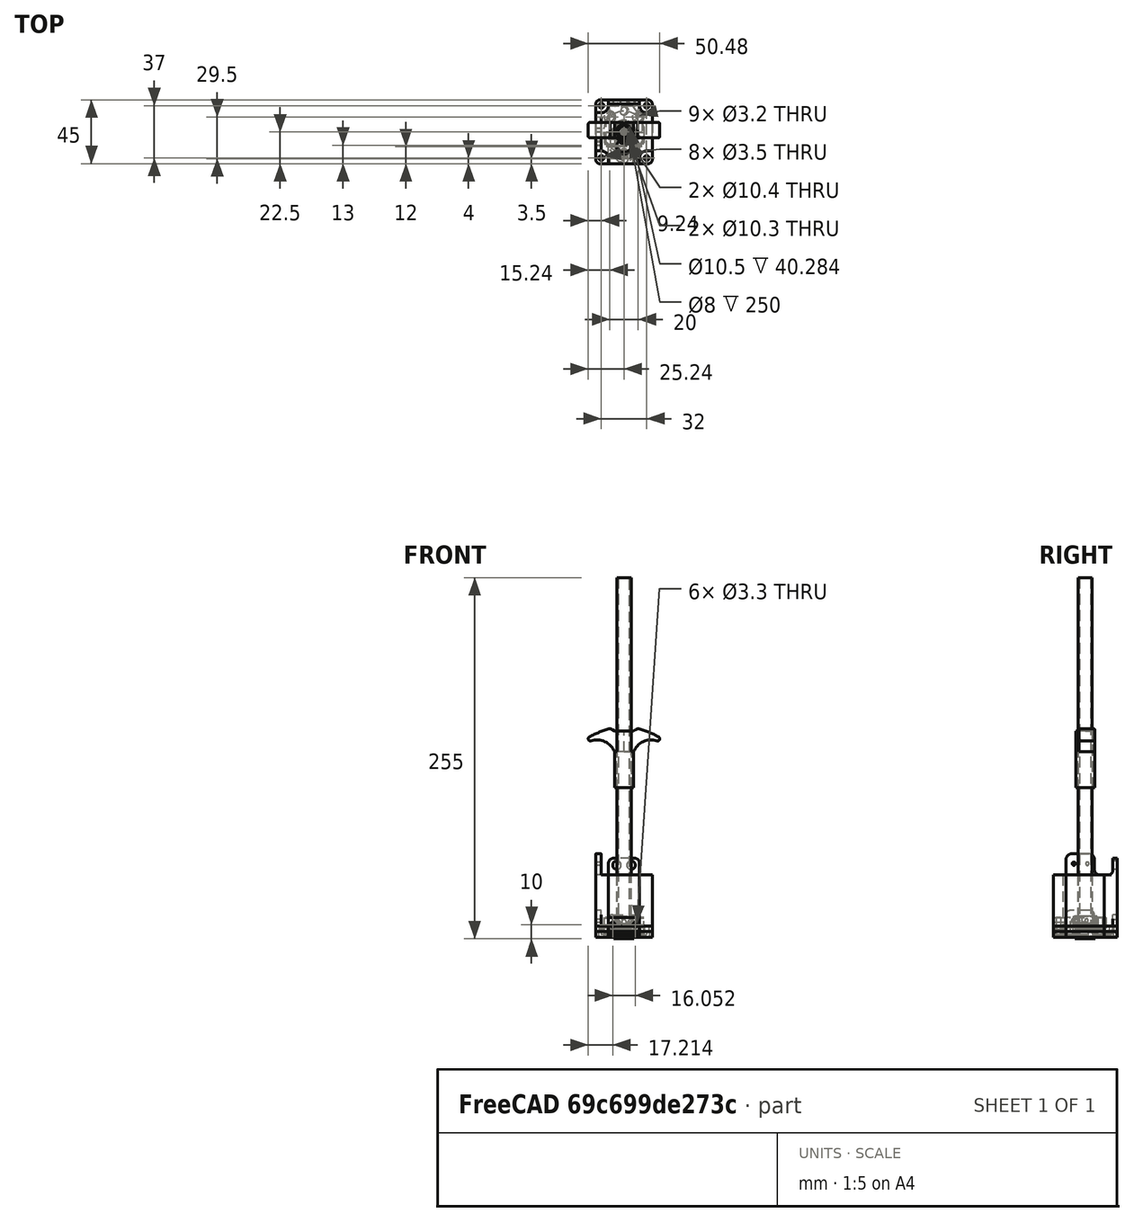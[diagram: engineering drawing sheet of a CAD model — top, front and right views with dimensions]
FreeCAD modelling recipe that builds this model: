
FCSTD DOCUMENT  (FreeCAD 1.0R39109 (Git))
Label: AltGearHandle
License: All rights reserved
LicenseURL: http://en.wikipedia.org/wiki/All_rights_reserved
objects: Sketcher::SketchObject×36, PartDesign::Pad×15, PartDesign::Body×14, PartDesign::Pocket×12, App::Link×9, App::FeaturePython×9, PartDesign::Fillet×8, PartDesign::Revolution×6, PartDesign::Chamfer×3, PartDesign::Hole×2, PartDesign::Mirrored×2, PartDesign::Plane×2, Part::Part2DObjectPython×2, Assembly::JointGroup×1, Assembly::AssemblyObject×1
note: 232 computed .brp shape members not serialized (recipe doc carries the construction recipe); baked Part::Feature solids carry a one-line shape summary decoded from their .brp

FEATURE [Sketcher::SketchObject] Sketch
  ArcFitTolerance = 0
  AttachmentSupport = -> [XY_Plane]
  FullyConstrained = true
  MakeInternals = false
  MapMode = 5
  sketch-geometry (11):
    g0: LineSegment StartX=-12.7 StartY=8.1026 StartZ=0 EndX=-5.7589 EndY=18.8369 EndZ=0
    g1: ArcOfCircle CenterX=0 CenterY=15.113 CenterZ=0 NormalX=0 NormalY=0 NormalZ=1 AngleXU=0 Radius=6.858 StartAngle=0.574002 EndAngle=2.56759
    g2: LineSegment StartX=5.7589 StartY=18.8369 StartZ=0 EndX=12.7 EndY=8.1026 EndZ=0
    g3: LineSegment StartX=12.7 StartY=8.1026 StartZ=0 EndX=12.7 EndY=-8.1026 EndZ=0
    g4: LineSegment StartX=12.7 StartY=-8.1026 StartZ=0 EndX=5.7589 EndY=-18.8369 EndZ=0
    g5: ArcOfCircle CenterX=0 CenterY=-15.113 CenterZ=0 NormalX=0 NormalY=0 NormalZ=1 AngleXU=0 Radius=6.858 StartAngle=3.71559 EndAngle=5.70918
    g6: LineSegment StartX=-5.7589 StartY=-18.8369 StartZ=0 EndX=-12.7 EndY=-8.1026 EndZ=0
    g7: LineSegment StartX=-12.7 StartY=-8.1026 StartZ=0 EndX=-12.7 EndY=8.1026 EndZ=0
    g8: LineSegment [constr] StartX=0 StartY=21.971 StartZ=0 EndX=12.7 EndY=21.971 EndZ=0
    g9: Circle CenterX=2.5146 CenterY=-3.2766 CenterZ=0 NormalX=0 NormalY=0 NormalZ=1 AngleXU=0 Radius=5.5
    g10: LineSegment [constr] StartX=0 StartY=-21.971 StartZ=0 EndX=12.7 EndY=-21.971 EndZ=0
  constraints (30):
    c: Tangent(g0,g1) = 1.5708
    c: Tangent(g1,g2) = 1.5708
    c: Coincident(g2,g3)
    c: Coincident(g3,g4)
    c: Tangent(g4,g5) = 1.5708
    c: Tangent(g5,g6) = 1.5708
    c: Coincident(g6,g7)
    c: Coincident(g7,g0)
    c: Vertical(g7)
    c: PointOnObject(g1,g-2)
    c: Equal(g5,g1)
    c: PointOnObject(g8,g-2)
    c: Horizontal(g8)
    c: Vertical(g8,g2)
    c: Tangent(g8,g1)
    c: DistanceY(g8) = 21.971
    c: Symmetric(g1,g5,g-1)
    c: Symmetric(g0,g2,g-2)
    c: Equal(g7,g3)
    c: Symmetric(g3,g2,g-1)
    c: Radius(g5) = 6.858
    c: DistanceY(g2,g8) = 13.8684
    c: DistanceX(g6,g3) = 25.4
    c: DistanceX(g9,g3) = 10.1854
    c: Diameter(g9) = 11
    c: PointOnObject(g10,g-2)
    c: Horizontal(g10)
    c: Equal(g10,g8)
    c: Tangent(g10,g5)
    c: DistanceY(g10,g9) = 18.6944
FEATURE [PartDesign::Pad] Pad  label="BasePad"
  Direction = (0,0,1)
  Length = 3.17
  Length2 = 10
  Profile = -> Sketch
  ReferenceAxis = -> Sketch [N_Axis]
  Reversed = true
  Suppressed = false
  Type = 0
FEATURE [Sketcher::SketchObject] Sketch001
  ArcFitTolerance = 0
  AttachmentSupport = -> [XY_Plane]
  ExternalGeometry = -> [Pad]
  FullyConstrained = true
  MakeInternals = false
  MapMode = 5
  sketch-geometry (3):
    g0: Circle CenterX=0 CenterY=15.113 CenterZ=0 NormalX=0 NormalY=0 NormalZ=1 AngleXU=0 Radius=2.3114
    g1: Circle CenterX=0 CenterY=-15.113 CenterZ=0 NormalX=0 NormalY=0 NormalZ=1 AngleXU=0 Radius=2.3114
    g2: LineSegment [constr] StartX=0 StartY=21.971 StartZ=0 EndX=5.7589 EndY=21.971 EndZ=0
  constraints (9):
    c: PointOnObject(g0,g-2)
    c: Horizontal(g2)
    c: PointOnObject(g2,g-2)
    c: Vertical(g2,g-3)
    c: Tangent(g2,g-3)
    c: Equal(g0,g1)
    c: Diameter(g0) = 4.6228
    c: Symmetric(g0,g1,g-1)
    c: DistanceY(g0,g2) = 6.858
FEATURE [PartDesign::Hole] Hole
  BaseFeature = -> Pad
  CustomThreadClearance = 0
  Depth = 25
  DepthType = 0
  Diameter = 4.5
  DrillForDepth = false
  DrillPoint = 1
  DrillPointAngle = 118
  HoleCutCountersinkAngle = 90
  HoleCutCustomValues = false
  HoleCutDepth = 0
  HoleCutDiameter = 6.3
  HoleCutType = 2
  ModelThread = false
  Profile = -> Sketch001
  Suppressed = false
  Tapered = false
  TaperedAngle = 90
  ThreadClass = 0
  ThreadDepth = 25
  ThreadDepthType = 0
  ThreadDirection = 0
  ThreadFit = 0
  ThreadSize = 11
  ThreadType = 1
  Threaded = false
  UseCustomThreadClearance = false
FEATURE [PartDesign::Fillet] Fillet
  Base = -> Hole [Edge13,Edge14,Edge6,Edge3]
  BaseFeature = -> Hole
  Radius = 1
  SupportTransform = false
  Suppressed = false
  UseAllEdges = false
FEATURE [PartDesign::Body] Body  label="mountingPlate"
  AllowCompound = false
  Group = -> [Sketch,Pad,Sketch001,Hole,Fillet]
  Origin = -> Origin
  Tip = -> Fillet
FEATURE [Sketcher::SketchObject] Sketch002  label="mastersketch"
  ArcFitTolerance = 0
  AttachmentSupport = -> [XZ_Plane001]
  FullyConstrained = false
  MakeInternals = false
  MapMode = 5
  Placement = pos=(0,0,0) rot=(1,0,0;1.5708rad)
  sketch-geometry (21):
    g0: LineSegment StartX=-5 StartY=101.6 StartZ=0 EndX=5 EndY=101.6 EndZ=0
    g1: LineSegment StartX=5 StartY=101.6 StartZ=0 EndX=5 EndY=-60 EndZ=0
    g2: LineSegment StartX=5 StartY=-60 StartZ=0 EndX=-5 EndY=-60 EndZ=0
    g3: LineSegment StartX=-5 StartY=-60 StartZ=0 EndX=-5 EndY=101.6 EndZ=0
    g4: LineSegment [constr] StartX=-25.4 StartY=0 StartZ=0 EndX=-25.4 EndY=147.32 EndZ=0
    g5: LineSegment [constr] StartX=25.4 StartY=0 StartZ=0 EndX=25.4 EndY=147.32 EndZ=0
    g6: LineSegment StartX=-6.70052 StartY=141.884 StartZ=0 EndX=6.70052 EndY=141.884 EndZ=0
    g7: LineSegment StartX=6.70052 StartY=141.884 StartZ=0 EndX=6.70052 EndY=101.6 EndZ=0
    g8: LineSegment StartX=6.70052 StartY=101.6 StartZ=0 EndX=-6.70052 EndY=101.6 EndZ=0
    g9: LineSegment StartX=-6.70052 StartY=101.6 StartZ=0 EndX=-6.70052 EndY=141.884 EndZ=0
    g10: ArcOfCircle CenterX=-19.1442 CenterY=122.136 CenterZ=0 NormalX=0 NormalY=0 NormalZ=1 AngleXU=0 Radius=13.3604 StartAngle=0.3726 EndAngle=1.90028
    g11: ArcOfCircle CenterX=-23.9395 CenterY=136.16 CenterZ=0 NormalX=0 NormalY=0 NormalZ=1 AngleXU=0 Radius=1.4605 StartAngle=1.94929 EndAngle=5.04187
    g12: LineSegment StartX=-24.4792 StartY=137.517 StartZ=0 EndX=-9.6647 EndY=143.408 EndZ=0
    g13: LineSegment StartX=-9.6647 StartY=143.408 StartZ=0 EndX=-6.70052 EndY=141.884 EndZ=0
    g14: LineSegment StartX=-6.70052 StartY=141.884 StartZ=0 EndX=-6.70052 EndY=127 EndZ=0
    g15: LineSegment StartX=6.70052 StartY=128.917 StartZ=0 EndX=6.70052 EndY=141.884 EndZ=0
    g16: LineSegment StartX=6.70052 StartY=141.884 StartZ=0 EndX=9.6647 EndY=143.408 EndZ=0
    g17: LineSegment StartX=9.6647 StartY=143.408 StartZ=0 EndX=24.4792 EndY=137.517 EndZ=0
    g18: ArcOfCircle CenterX=23.9395 CenterY=136.16 CenterZ=0 NormalX=0 NormalY=0 NormalZ=1 AngleXU=0 Radius=1.4605 StartAngle=4.38291 EndAngle=7.47549
    g19: ArcOfCircle CenterX=19.1442 CenterY=122.136 CenterZ=0 NormalX=0 NormalY=0 NormalZ=1 AngleXU=0 Radius=13.3604 StartAngle=1.24132 EndAngle=2.76899
    g20: LineSegment StartX=6.70052 StartY=127 StartZ=0 EndX=6.70052 EndY=141.884 EndZ=0
  constraints (58):
    c: Coincident(g0,g1)
    c: Coincident(g1,g2)
    c: Coincident(g2,g3)
    c: Coincident(g3,g0)
    c: Horizontal(g0)
    c: Vertical(g1)
    c: Vertical(g3)
    c: Symmetric(g2,g1,g-2)
    c: DistanceX(g2,g2) = 10
    c: DistanceY(g0) = 101.6
    c: DistanceY(g1) = -60
    c: PointOnObject(g4,g-1)
    c: Vertical(g4)
    c: PointOnObject(g5,g-1)
    c: Vertical(g5)
    c: Symmetric(g5,g4,g-2)
    c: DistanceX(g4,g5) = 50.8
    c: DistanceY(g0,g5) = 45.72
    c: Coincident(g6,g7)
    c: Coincident(g7,g8)
    c: Coincident(g8,g9)
    c: Coincident(g9,g6)
    c: Horizontal(g6)
    c: Vertical(g7)
    c: Vertical(g9)
    c: Horizontal(g0,g7)
    c: Symmetric(g8,g7,g-2)
    c: DistanceX(g8,g8) = 13.401
    c: DistanceY(g6,g5) = 5.4356
    c: PointOnObject(g10,g9)
    c: Tangent(g10,g11) = 1.5708
    c: Tangent(g11,g12) = 1.5708
    c: Coincident(g12,g13)
    c: Coincident(g13,g14)
    c: Coincident(g14,g10)
    c: PointOnObject(g15,g7)
    c: PointOnObject(g15,g7)
    c: Coincident(g15,g16)
    c: Coincident(g16,g17)
    c: Tangent(g17,g18) = 1.5708
    c: Tangent(g18,g19) = 1.5708
    c: PointOnObject(g19,g7)
    c: Coincident(g20,g19)
    c: Coincident(g20,g15)
    c: Horizontal(g19,g10)
    c: Equal(g10,g19)
    c: Equal(g18,g11)
    c: Tangent(g18,g5)
    c: Symmetric(g18,g11,g-2)
    c: Horizontal(g13,g15)
    c: Symmetric(g16,g12,g-2)
    c: Radius(g19) = 13.3604
    c: Radius(g18) = 1.4605
    c: DistanceY(g8,g10) = 25.4
    c: DistanceY(g6,g16) = 1.524
    c: Coincident(g13,g6)
    c: DistanceX(g12,g16) = 19.3294
    c: DistanceY(g10,g11) = 9.16
FEATURE [Sketcher::SketchObject] Sketch004
  ArcFitTolerance = 0
  AttachmentOffset = pos=(0,0,-6.7) rot=(0,0,1;0rad)
  AttachmentSupport = -> [XZ_Plane001]
  ExternalGeometry = -> [Sketch002]
  FullyConstrained = true
  MakeInternals = false
  MapMode = 5
  Placement = pos=(0,6.7,-1.5e-15) rot=(1,0,0;1.5708rad)
  sketch-geometry (7):
    g0: LineSegment StartX=-6.70052 StartY=141.884 StartZ=0 EndX=-9.6647 EndY=143.408 EndZ=0
    g1: ArcOfCircle CenterX=-19.1442 CenterY=122.136 CenterZ=0 NormalX=0 NormalY=0 NormalZ=1 AngleXU=0 Radius=13.3604 StartAngle=0.3726 EndAngle=1.8879
    g2: LineSegment StartX=-6.70052 StartY=141.884 StartZ=0 EndX=0 EndY=141.884 EndZ=0
    g3: LineSegment StartX=0 StartY=141.884 StartZ=0 EndX=0 EndY=127 EndZ=0
    g4: LineSegment StartX=0 StartY=127 StartZ=0 EndX=-6.70052 EndY=127 EndZ=0
    g5: ArcOfCircle CenterX=6.31595 CenterY=81.6504 CenterZ=0 NormalX=0 NormalY=0 NormalZ=1 AngleXU=0 Radius=63.7921 StartAngle=1.824 EndAngle=2.07458
    g6: ArcOfCircle CenterX=-23.7689 CenterY=136.229 CenterZ=0 NormalX=0 NormalY=0 NormalZ=1 AngleXU=0 Radius=1.47134 StartAngle=2.07458 EndAngle=5.02949
  constraints (18):
    c: Coincident(g1,g-4)
    c: Coincident(g0,g-6)
    c: Parallel(g-6,g0)
    c: Coincident(g1,g-4)
    c: Coincident(g0,g2)
    c: Horizontal(g2)
    c: Coincident(g2,g3)
    c: Vertical(g3)
    c: Coincident(g3,g4)
    c: Coincident(g4,g1)
    c: Horizontal(g4)
    c: Horizontal(g0,g-6)
    c: PointOnObject(g2,g-2)
    c: Coincident(g5,g0)
    c: Radius(g5) = 63.7921
    c: Tangent(g6,g5) = -1.5708
    c: Tangent(g6,g1) = 1.5708
    c: Coincident(g-5,g5)
FEATURE [PartDesign::Pad] Pad001  label="gripBase1"
  Direction = (0,-1,2e-16)
  Length = 11
  Length2 = 10
  Placement = pos=(0,0,0) rot=(1,0,0;1.5708rad)
  Profile = -> Sketch004
  ReferenceAxis = -> Sketch004 [N_Axis]
  Suppressed = false
  Type = 0
FEATURE [PartDesign::Mirrored] Mirrored
  BaseFeature = -> Pad001
  MirrorPlane = -> Sketch004 [V_Axis]
  Originals = -> [Pad001]
  Placement = pos=(0,0,0) rot=(1,0,0;1.5708rad)
  Suppressed = false
  TransformMode = 0
FEATURE [PartDesign::Fillet] Fillet001  label="Grip"
  Base = -> Mirrored [Edge25,Edge29,Edge16,Edge11]
  BaseFeature = -> Mirrored
  Placement = pos=(0,0,0) rot=(1,0,0;1.5708rad)
  Radius = 1.2
  SupportTransform = false
  Suppressed = false
  UseAllEdges = false
FEATURE [Sketcher::SketchObject] Sketch005
  ArcFitTolerance = 0
  AttachmentSupport = -> [XZ_Plane001]
  ExternalGeometry = -> [Sketch002]
  FullyConstrained = true
  MakeInternals = false
  MapMode = 5
  Placement = pos=(0,0,0) rot=(1,0,0;1.5708rad)
  sketch-geometry (4):
    g0: LineSegment StartX=-6.70052 StartY=141.884 StartZ=0 EndX=0 EndY=141.884 EndZ=0
    g1: LineSegment StartX=0 StartY=141.884 StartZ=0 EndX=0 EndY=101.6 EndZ=0
    g2: LineSegment StartX=0 StartY=101.6 StartZ=0 EndX=-6.70052 EndY=101.6 EndZ=0
    g3: LineSegment StartX=-6.70052 StartY=101.6 StartZ=0 EndX=-6.70052 EndY=141.884 EndZ=0
  constraints (11):
    c: Coincident(g0,g1)
    c: Coincident(g1,g2)
    c: Coincident(g2,g3)
    c: Coincident(g3,g0)
    c: Horizontal(g0)
    c: Horizontal(g2)
    c: Vertical(g1)
    c: Vertical(g3)
    c: Coincident(g0,g-3)
    c: PointOnObject(g1,g-2)
    c: Horizontal(g-3,g1)
FEATURE [PartDesign::Revolution] Revolution
  Angle = 360
  Angle2 = 60
  Axis = (0,2e-16,1)
  Base = (0,0,0)
  BaseFeature = -> Fillet001
  Placement = pos=(0,0,0) rot=(1,0,0;1.5708rad)
  Profile = -> Sketch005
  ReferenceAxis = -> Sketch005 [V_Axis]
  Suppressed = false
  Type = 0
FEATURE [Sketcher::SketchObject] Sketch006
  ArcFitTolerance = 0
  AttachmentSupport = -> [XY_Plane001]
  ExternalGeometry = -> [Sketch002]
  FullyConstrained = true
  MakeInternals = false
  MapMode = 5
  sketch-geometry (1):
    g0: Circle CenterX=0 CenterY=0 CenterZ=0 NormalX=0 NormalY=0 NormalZ=1 AngleXU=0 Radius=5.25
  constraints (2):
    c: Coincident(g0,g-1)
    c: Diameter(g0) = 10.5
FEATURE [PartDesign::Pocket] Pocket
  BaseFeature = -> Revolution
  Direction = (0,0,-1)
  Length = 5
  Length2 = 5
  Midplane = true
  Placement = pos=(0,0,0) rot=(1,0,0;1.5708rad)
  Profile = -> Sketch006
  ReferenceAxis = -> Sketch006 [N_Axis]
  Suppressed = false
  Type = 1
FEATURE [PartDesign::Plane] DatumPlane
  AttachmentSupport = -> [Pocket]
  Length = 60.0479
  MapMode = 45
  Placement = pos=(0,6.70021,141.884) rot=(0,0,1;1.5708rad)
  ResizeMode = 0
  Width = 60.5283
FEATURE [PartDesign::Plane] DatumPlane001
  AttachmentSupport = -> [Pocket]
  Length = 193.249
  MapMode = 45
  Placement = pos=(-24.6781,1.2,135.833) rot=(0.548172,0,0.836366;3.14159rad)
  ResizeMode = 0
  Width = 68.6849
FEATURE [PartDesign::Body] Body001  label="Handle"
  AllowCompound = false
  Group = -> [Sketch002,Sketch004,Pad001,Mirrored,Fillet001,Sketch005,Revolution,Sketch006,Pocket,DatumPlane,DatumPlane001]
  Origin = -> Origin001
  Tip = -> Pocket
FEATURE [Sketcher::SketchObject] Sketch008
  ArcFitTolerance = 1e-06
  AttachmentSupport = -> [XZ_Plane003]
  FullyConstrained = true
  MakeInternals = false
  MapMode = 5
  Placement = pos=(0,0,0) rot=(1,0,0;1.5708rad)
  sketch-geometry (12):
    g0: LineSegment StartX=-3.6 StartY=0 StartZ=0 EndX=-3.6 EndY=2.452 EndZ=0
    g1: LineSegment StartX=-3.6 StartY=2.452 StartZ=0 EndX=-4.699 EndY=2.452 EndZ=0
    g2: LineSegment StartX=-4.699 StartY=2.452 StartZ=0 EndX=-4.699 EndY=5.5 EndZ=0
    g3: LineSegment StartX=-4.699 StartY=5.5 StartZ=0 EndX=0 EndY=5.5 EndZ=0
    g4: LineSegment StartX=0 StartY=5.5 StartZ=0 EndX=0 EndY=4 EndZ=0
    g5: LineSegment StartX=0 StartY=4 StartZ=0 EndX=-1.3 EndY=4 EndZ=0
    g6: LineSegment StartX=-1.3 StartY=4 StartZ=0 EndX=-1.3 EndY=1 EndZ=0
    g7: LineSegment StartX=-1.3 StartY=1 StartZ=0 EndX=-2.3 EndY=1 EndZ=0
    g8: LineSegment StartX=-2.3 StartY=1 StartZ=0 EndX=-2.3 EndY=4 EndZ=0
    g9: LineSegment StartX=-2.3 StartY=4 StartZ=0 EndX=-3.1 EndY=4 EndZ=0
    g10: LineSegment StartX=-3.1 StartY=4 StartZ=0 EndX=-3.1 EndY=0 EndZ=0
    g11: LineSegment StartX=-3.1 StartY=0 StartZ=0 EndX=-3.6 EndY=0 EndZ=0
  constraints (36):
    c: PointOnObject(g0,g-1)
    c: Vertical(g0)
    c: Coincident(g0,g1)
    c: Horizontal(g1)
    c: Coincident(g1,g2)
    c: Vertical(g2)
    c: Coincident(g2,g3)
    c: PointOnObject(g3,g-2)
    c: Horizontal(g3)
    c: Coincident(g3,g4)
    c: Vertical(g4)
    c: Coincident(g4,g5)
    c: Coincident(g5,g6)
    c: Coincident(g6,g7)
    c: Coincident(g7,g8)
    c: Vertical(g8)
    c: Coincident(g8,g9)
    c: Coincident(g9,g10)
    c: Vertical(g10)
    c: Coincident(g10,g11)
    c: Coincident(g11,g0)
    c: Horizontal(g11)
    c: Horizontal(g7)
    c: Vertical(g6)
    c: Horizontal(g5)
    c: DistanceY(g2,g2) = 3.048
    c: Horizontal(g5,g8)
    c: Horizontal(g9)
    c: DistanceY(g6,g6) = 3
    c: DistanceX(g5,g5) = 1.3
    c: DistanceX(g3,g3) = 4.699
    c: DistanceX(g7,g7) = 1
    c: DistanceY(g4,g4) = 1.5
    c: DistanceY(g10,g7) = 1
    c: DistanceX(g9,g9) = 0.8
    c: DistanceX(g11,g11) = 0.5
FEATURE [Sketcher::SketchObject] Sketch009
  ArcFitTolerance = 1e-06
  AttachmentSupport = -> [XZ_Plane002]
  FullyConstrained = true
  MakeInternals = false
  MapMode = 5
  Placement = pos=(0,0,0) rot=(1,0,0;1.5708rad)
  sketch-geometry (6):
    g0: LineSegment StartX=-3.25 StartY=0 StartZ=0 EndX=-3.25 EndY=6 EndZ=0
    g1: LineSegment StartX=-5.1 StartY=4.476 StartZ=0 EndX=-4.9 EndY=0 EndZ=0
    g2: LineSegment StartX=-4.9 StartY=0 StartZ=0 EndX=-3.25 EndY=0 EndZ=0
    g3: LineSegment StartX=-5.1 StartY=4.476 StartZ=0 EndX=-6 EndY=4.476 EndZ=0
    g4: LineSegment StartX=-6 StartY=4.476 StartZ=0 EndX=-6 EndY=6 EndZ=0
    g5: LineSegment StartX=-6 StartY=6 StartZ=0 EndX=-3.25 EndY=6 EndZ=0
  constraints (18):
    c: PointOnObject(g2,g-1)
    c: PointOnObject(g1,g-1)
    c: Coincident(g1,g2)
    c: Coincident(g1,g3)
    c: Coincident(g3,g4)
    c: Vertical(g4)
    c: Horizontal(g3)
    c: DistanceY(g4,g4) = 1.524
    c: DistanceX(g1) = -4.9
    c: DistanceX(g1) = -5.1
    c: DistanceX(g4) = -6
    c: Coincident(g0,g2)
    c: Vertical(g0)
    c: Coincident(g5,g4)
    c: Coincident(g5,g0)
    c: Horizontal(g5)
    c: DistanceX(g0) = -3.25
    c: DistanceY(g0,g0) = 6
FEATURE [PartDesign::Revolution] Revolution001
  Angle = 360
  Angle2 = 60
  Axis = (0,2e-16,1)
  Base = (0,0,0)
  Placement = pos=(0,0,0) rot=(1,0,0;1.5708rad)
  Profile = -> Sketch009
  ReferenceAxis = -> Sketch009 [V_Axis]
  Suppressed = false
  Type = 0
FEATURE [PartDesign::Body] Body002  label="TopNut"
  AllowCompound = false
  Group = -> [Sketch009,Revolution001]
  Origin = -> Origin002
  Tip = -> Revolution001
FEATURE [PartDesign::Revolution] Revolution002
  Angle = 360
  Angle2 = 60
  Axis = (0,2e-16,1)
  Base = (0,0,0)
  Placement = pos=(0,0,0) rot=(1,0,0;1.5708rad)
  Profile = -> Sketch008
  ReferenceAxis = -> Sketch008 [V_Axis]
  Suppressed = false
  Type = 0
FEATURE [Sketcher::SketchObject] Sketch010
  ArcFitTolerance = 1e-06
  AttachmentSupport = -> [XY_Plane003]
  FullyConstrained = true
  MakeInternals = false
  MapMode = 5
  sketch-geometry (4):
    g0: LineSegment StartX=-0.25 StartY=2.5 StartZ=0 EndX=-0.25 EndY=-2.5 EndZ=0
    g1: LineSegment StartX=-0.25 StartY=-2.5 StartZ=0 EndX=0.25 EndY=-2.5 EndZ=0
    g2: LineSegment StartX=0.25 StartY=-2.5 StartZ=0 EndX=0.25 EndY=2.5 EndZ=0
    g3: LineSegment StartX=0.25 StartY=2.5 StartZ=0 EndX=-0.25 EndY=2.5 EndZ=0
  constraints (11):
    c: Coincident(g0,g1)
    c: Coincident(g1,g2)
    c: Coincident(g2,g3)
    c: Coincident(g3,g0)
    c: Vertical(g0)
    c: Vertical(g2)
    c: Horizontal(g1)
    c: Horizontal(g3)
    c: Symmetric(g0,g2,g-1)
    c: DistanceY(g2,g2) = 5
    c: DistanceX(g1,g1) = 0.5
FEATURE [PartDesign::Pocket] Pocket001
  BaseFeature = -> Revolution002
  Direction = (0,0,-1)
  Length = 0
  Length2 = 5
  Placement = pos=(0,0,0) rot=(1,0,0;1.5708rad)
  Profile = -> Sketch010
  ReferenceAxis = -> Sketch010 [N_Axis]
  Reversed = true
  Suppressed = false
  Type = 3
  UpToFace = -> Revolution002 [Face5]
FEATURE [PartDesign::Chamfer] Chamfer
  Angle = 45
  Base = -> Pocket001 [Edge8,Edge5,Edge42,Edge29]
  BaseFeature = -> Pocket001
  ChamferType = 0
  FlipDirection = false
  Placement = pos=(0,0,0) rot=(1,0,0;1.5708rad)
  Size = 0.3
  Size2 = 1
  SupportTransform = false
  Suppressed = false
  UseAllEdges = false
FEATURE [PartDesign::Body] Body003  label="Button"
  AllowCompound = false
  Group = -> [Sketch008,Revolution002,Sketch010,Pocket001,Chamfer]
  Origin = -> Origin003
  Tip = -> Chamfer
FEATURE [Sketcher::SketchObject] Sketch011
  ArcFitTolerance = 1e-06
  AttachmentSupport = -> [XZ_Plane004]
  FullyConstrained = true
  MakeInternals = false
  MapMode = 5
  Placement = pos=(0,0,0) rot=(1,0,0;1.5708rad)
  sketch-geometry (12):
    g0: LineSegment StartX=-3.45 StartY=0 StartZ=0 EndX=-3.45 EndY=1.452 EndZ=0
    g1: LineSegment StartX=-3.45 StartY=1.452 StartZ=0 EndX=-4.699 EndY=1.452 EndZ=0
    g2: LineSegment StartX=-4.699 StartY=1.452 StartZ=0 EndX=-4.699 EndY=4.5 EndZ=0
    g3: LineSegment StartX=-4.699 StartY=4.5 StartZ=0 EndX=0 EndY=4.5 EndZ=0
    g4: LineSegment StartX=0 StartY=4.5 StartZ=0 EndX=0 EndY=3 EndZ=0
    g5: LineSegment StartX=0 StartY=3 StartZ=0 EndX=-1.15 EndY=3 EndZ=0
    g6: LineSegment StartX=-1.15 StartY=3 StartZ=0 EndX=-1.15 EndY=0 EndZ=0
    g7: LineSegment StartX=-1.15 StartY=0 StartZ=0 EndX=-2.15 EndY=0 EndZ=0
    g8: LineSegment StartX=-2.15 StartY=0 StartZ=0 EndX=-2.15 EndY=3 EndZ=0
    g9: LineSegment StartX=-2.15 StartY=3 StartZ=0 EndX=-2.95 EndY=3 EndZ=0
    g10: LineSegment StartX=-2.95 StartY=3 StartZ=0 EndX=-2.95 EndY=0 EndZ=0
    g11: LineSegment StartX=-2.95 StartY=0 StartZ=0 EndX=-3.45 EndY=0 EndZ=0
  constraints (36):
    c: Vertical(g0)
    c: Coincident(g0,g1)
    c: Horizontal(g1)
    c: Coincident(g1,g2)
    c: Vertical(g2)
    c: Coincident(g2,g3)
    c: PointOnObject(g3,g-2)
    c: Horizontal(g3)
    c: Coincident(g3,g4)
    c: Vertical(g4)
    c: Coincident(g4,g5)
    c: Coincident(g5,g6)
    c: Coincident(g6,g7)
    c: Coincident(g7,g8)
    c: Vertical(g8)
    c: Coincident(g8,g9)
    c: Coincident(g9,g10)
    c: Vertical(g10)
    c: Coincident(g10,g11)
    c: Coincident(g11,g0)
    c: Horizontal(g11)
    c: Horizontal(g7)
    c: Vertical(g6)
    c: Horizontal(g5)
    c: DistanceY(g2,g2) = 3.048
    c: Horizontal(g5,g8)
    c: Horizontal(g9)
    c: DistanceY(g6,g6) = 3
    c: DistanceX(g5,g5) = 1.15
    c: DistanceX(g3,g3) = 4.699
    c: DistanceX(g7,g7) = 1
    c: DistanceY(g4,g4) = 1.5
    c: DistanceX(g9,g9) = 0.8
    c: DistanceX(g11,g11) = 0.5
    c: Horizontal(g10,g7)
    c: PointOnObject(g10,g-1)
FEATURE [PartDesign::Revolution] Revolution003
  Angle = 360
  Angle2 = 60
  Axis = (0,2e-16,1)
  Base = (0,0,0)
  Placement = pos=(0,0,0) rot=(1,0,0;1.5708rad)
  Profile = -> Sketch011
  ReferenceAxis = -> Sketch011 [V_Axis]
  Suppressed = false
  Type = 0
FEATURE [Sketcher::SketchObject] Sketch012
  ArcFitTolerance = 1e-06
  AttachmentSupport = -> [XY_Plane004]
  FullyConstrained = true
  MakeInternals = false
  MapMode = 5
  sketch-geometry (4):
    g0: LineSegment StartX=-0.25 StartY=2.5 StartZ=0 EndX=-0.25 EndY=-2.5 EndZ=0
    g1: LineSegment StartX=-0.25 StartY=-2.5 StartZ=0 EndX=0.25 EndY=-2.5 EndZ=0
    g2: LineSegment StartX=0.25 StartY=-2.5 StartZ=0 EndX=0.25 EndY=2.5 EndZ=0
    g3: LineSegment StartX=0.25 StartY=2.5 StartZ=0 EndX=-0.25 EndY=2.5 EndZ=0
  constraints (11):
    c: Coincident(g0,g1)
    c: Coincident(g1,g2)
    c: Coincident(g2,g3)
    c: Coincident(g3,g0)
    c: Vertical(g0)
    c: Vertical(g2)
    c: Horizontal(g1)
    c: Horizontal(g3)
    c: Symmetric(g0,g2,g-1)
    c: DistanceY(g2,g2) = 5
    c: DistanceX(g1,g1) = 0.5
FEATURE [PartDesign::Pocket] Pocket002
  BaseFeature = -> Revolution003
  Direction = (0,0,-1)
  Length = 0
  Length2 = 5
  Placement = pos=(0,0,0) rot=(1,0,0;1.5708rad)
  Profile = -> Sketch012
  ReferenceAxis = -> Sketch012 [N_Axis]
  Reversed = true
  Suppressed = false
  Type = 3
  UpToFace = -> Revolution003 [Face5]
FEATURE [PartDesign::Chamfer] Chamfer001
  Angle = 45
  Base = -> Pocket002 [Edge8,Edge5,Edge42,Edge29]
  BaseFeature = -> Pocket002
  ChamferType = 0
  FlipDirection = false
  Placement = pos=(0,0,0) rot=(1,0,0;1.5708rad)
  Size = 0.3
  Size2 = 1
  SupportTransform = false
  Suppressed = false
  UseAllEdges = false
FEATURE [PartDesign::Body] Body004  label="Button2"
  AllowCompound = false
  Group = -> [Sketch011,Revolution003,Sketch012,Pocket002,Chamfer001]
  Origin = -> Origin004
  Tip = -> Chamfer001
FEATURE [Sketcher::SketchObject] Sketch013
  ArcFitTolerance = 1e-06
  AttachmentSupport = -> [XY_Plane005]
  FullyConstrained = true
  MakeInternals = false
  MapMode = 5
  sketch-geometry (13):
    g0: LineSegment StartX=-20 StartY=22.5 StartZ=0 EndX=-20 EndY=-22.5 EndZ=0
    g1: LineSegment StartX=-20 StartY=-22.5 StartZ=0 EndX=20 EndY=-22.5 EndZ=0
    g2: LineSegment StartX=20 StartY=-22.5 StartZ=0 EndX=20 EndY=22.5 EndZ=0
    g3: LineSegment StartX=20 StartY=22.5 StartZ=0 EndX=-20 EndY=22.5 EndZ=0
    g4: LineSegment [constr] StartX=-16 StartY=18.5 StartZ=0 EndX=-16 EndY=-18.5 EndZ=0
    g5: LineSegment [constr] StartX=-16 StartY=-18.5 StartZ=0 EndX=16 EndY=-18.5 EndZ=0
    g6: LineSegment [constr] StartX=16 StartY=-18.5 StartZ=0 EndX=16 EndY=18.5 EndZ=0
    g7: LineSegment [constr] StartX=16 StartY=18.5 StartZ=0 EndX=-16 EndY=18.5 EndZ=0
    g8: Circle CenterX=-16 CenterY=18.5 CenterZ=0 NormalX=0 NormalY=0 NormalZ=1 AngleXU=0 Radius=1.75
    g9: Circle CenterX=16 CenterY=18.5 CenterZ=0 NormalX=0 NormalY=0 NormalZ=1 AngleXU=0 Radius=1.75
    g10: Circle CenterX=16 CenterY=-18.5 CenterZ=0 NormalX=0 NormalY=0 NormalZ=1 AngleXU=0 Radius=1.75
    g11: Circle CenterX=-16 CenterY=-18.5 CenterZ=0 NormalX=0 NormalY=0 NormalZ=1 AngleXU=0 Radius=1.75
    g12: Circle CenterX=0 CenterY=-10.5 CenterZ=0 NormalX=0 NormalY=0 NormalZ=1 AngleXU=0 Radius=5.2
  constraints (33):
    c: Coincident(g0,g1)
    c: Coincident(g1,g2)
    c: Coincident(g2,g3)
    c: Coincident(g3,g0)
    c: Vertical(g0)
    c: Vertical(g2)
    c: Horizontal(g1)
    c: Horizontal(g3)
    c: Symmetric(g0,g1,g-1)
    c: Coincident(g4,g5)
    c: Coincident(g5,g6)
    c: Coincident(g6,g7)
    c: Coincident(g7,g4)
    c: Vertical(g4)
    c: Vertical(g6)
    c: Horizontal(g5)
    c: Horizontal(g7)
    c: DistanceX(g0,g4) = 4
    c: DistanceY(g4,g0) = 4
    c: Coincident(g8,g4)
    c: Coincident(g9,g6)
    c: Coincident(g10,g5)
    c: Coincident(g11,g4)
    c: Equal(g8,g9)
    c: Equal(g9,g10)
    c: Equal(g10,g11)
    c: Diameter(g8) = 3.5
    c: PointOnObject(g12,g-2)
    c: Diameter(g12) = 10.4
    c: Symmetric(g5,g4,g-1)
    c: DistanceY(g2,g2) = 45
    c: DistanceX(g3,g3) = 40
    c: DistanceY(g1,g12) = 12
FEATURE [PartDesign::Pad] Pad002  label="FrontPad002"
  Direction = (0,0,1)
  Length = 4
  Length2 = 10
  Profile = -> Sketch013
  ReferenceAxis = -> Sketch013 [N_Axis]
  Reversed = true
  Suppressed = false
  Type = 0
FEATURE [PartDesign::Fillet] Fillet002
  Base = -> Pad002 [Edge8,Edge2,Edge1,Edge5]
  BaseFeature = -> Pad002
  Radius = 3
  SupportTransform = false
  Suppressed = false
  UseAllEdges = false
FEATURE [Sketcher::SketchObject] Sketch014
  ArcFitTolerance = 1e-06
  AttachmentSupport = -> [XY_Plane005]
  ExternalGeometry = -> [Fillet002]
  FullyConstrained = true
  MakeInternals = false
  MapMode = 5
  sketch-geometry (17):
    g0: Circle CenterX=0 CenterY=-10.5 CenterZ=0 NormalX=0 NormalY=0 NormalZ=1 AngleXU=0 Radius=5.2
    g1: LineSegment StartX=-20 StartY=-13.5 StartZ=0 EndX=-20 EndY=13.5 EndZ=0
    g2: LineSegment StartX=20 StartY=13.5 StartZ=0 EndX=20 EndY=-13.5 EndZ=0
    g3: LineSegment StartX=11 StartY=-22.5 StartZ=0 EndX=-11 EndY=-22.5 EndZ=0
    g4: LineSegment StartX=-11 StartY=22.5 StartZ=0 EndX=11 EndY=22.5 EndZ=0
    g5: LineSegment StartX=-20 StartY=13.5 StartZ=0 EndX=-16 EndY=13.5 EndZ=0
    g6: LineSegment StartX=-11 StartY=22.5 StartZ=0 EndX=-11 EndY=18.5 EndZ=0
    g7: LineSegment StartX=-20 StartY=-13.5 StartZ=0 EndX=-16 EndY=-13.5 EndZ=0
    g8: LineSegment StartX=-11 StartY=-22.5 StartZ=0 EndX=-11 EndY=-18.5 EndZ=0
    g9: LineSegment StartX=11 StartY=-22.5 StartZ=0 EndX=11 EndY=-18.5 EndZ=0
    g10: LineSegment StartX=20 StartY=-13.5 StartZ=0 EndX=16 EndY=-13.5 EndZ=0
    g11: LineSegment StartX=20 StartY=13.5 StartZ=0 EndX=16 EndY=13.5 EndZ=0
    g12: LineSegment StartX=11 StartY=22.5 StartZ=0 EndX=11 EndY=18.5 EndZ=0
    g13: ArcOfCircle CenterX=-16 CenterY=-18.5 CenterZ=0 NormalX=0 NormalY=0 NormalZ=1 AngleXU=0 Radius=5 StartAngle=3.895e-12 EndAngle=1.5708
    g14: ArcOfCircle CenterX=16 CenterY=-18.5 CenterZ=0 NormalX=0 NormalY=0 NormalZ=1 AngleXU=0 Radius=5 StartAngle=1.5708 EndAngle=3.14159
    g15: ArcOfCircle CenterX=-16 CenterY=18.5 CenterZ=0 NormalX=0 NormalY=0 NormalZ=1 AngleXU=0 Radius=5 StartAngle=4.71239 EndAngle=6.28319
    g16: ArcOfCircle CenterX=16 CenterY=18.5 CenterZ=0 NormalX=0 NormalY=0 NormalZ=1 AngleXU=0 Radius=5 StartAngle=3.14159 EndAngle=4.71239
  constraints (49):
    c: Coincident(g0,g-3)
    c: Equal(g-3,g0)
    c: PointOnObject(g3,g-4)
    c: Symmetric(g3,g3,g-2)
    c: Symmetric(g1,g2,g-2)
    c: Symmetric(g1,g2,g-2)
    c: Symmetric(g4,g4,g-2)
    c: PointOnObject(g4,g-5)
    c: Vertical(g4,g3)
    c: PointOnObject(g1,g-6)
    c: Symmetric(g1,g1,g-1)
    c: Coincident(g5,g1)
    c: Coincident(g6,g4)
    c: Coincident(g7,g1)
    c: Horizontal(g7)
    c: Coincident(g8,g3)
    c: Vertical(g8)
    c: Coincident(g9,g3)
    c: Vertical(g9)
    c: Coincident(g10,g2)
    c: Horizontal(g10)
    c: Coincident(g11,g2)
    c: Horizontal(g11)
    c: Coincident(g12,g4)
    c: Vertical(g12)
    c: Vertical(g6)
    c: Horizontal(g5)
    c: Vertical(g5,g-8)
    c: Horizontal(g6,g-8)
    c: Equal(g5,g11)
    c: Equal(g11,g10)
    c: Equal(g10,g7)
    c: Equal(g6,g12)
    c: Equal(g12,g9)
    c: Equal(g9,g8)
    c: Coincident(g13,g-7)
    c: Coincident(g13,g8)
    c: Coincident(g13,g7)
    c: Radius(g13) = 5
    c: Coincident(g14,g-10)
    c: Equal(g13,g14)
    c: Horizontal(g14,g8)
    c: Vertical(g14,g11)
    c: Coincident(g15,g-8)
    c: Coincident(g15,g5)
    c: Horizontal(g15,g15)
    c: Coincident(g16,g-9)
    c: Coincident(g16,g11)
    c: Horizontal(g16,g16)
FEATURE [PartDesign::Pad] Pad003  label="BodyPad003"
  BaseFeature = -> Fillet002
  Direction = (0,0,1)
  Length = 40
  Length2 = 10
  Profile = -> Sketch014
  ReferenceAxis = -> Sketch014 [N_Axis]
  Suppressed = false
  Type = 0
FEATURE [Sketcher::SketchObject] Sketch015
  ArcFitTolerance = 1e-06
  AttachmentSupport = -> [Pad003]
  ExternalGeometry = -> [Pad003]
  FullyConstrained = true
  MakeInternals = false
  MapMode = 5
  Placement = pos=(0,0,40) rot=(0,0,1;0rad)
  sketch-geometry (10):
    g0: Circle [constr] CenterX=0 CenterY=-10.5 CenterZ=0 NormalX=0 NormalY=0 NormalZ=1 AngleXU=0 Radius=7.2
    g1: Circle [constr] CenterX=0 CenterY=-10.5 CenterZ=0 NormalX=0 NormalY=0 NormalZ=1 AngleXU=0 Radius=14.5
    g2: LineSegment StartX=-20 StartY=-13.5 StartZ=0 EndX=-16 EndY=-13.5 EndZ=0
    g3: LineSegment StartX=-16 StartY=-13.5 StartZ=0 EndX=-16 EndY=6.5 EndZ=0
    g4: LineSegment StartX=-16 StartY=6.5 StartZ=0 EndX=-20 EndY=6.5 EndZ=0
    g5: LineSegment StartX=-20 StartY=6.5 StartZ=0 EndX=-20 EndY=-13.5 EndZ=0
    g6: LineSegment [constr] StartX=-16 StartY=6.5 StartZ=0 EndX=-16 EndY=-13.5 EndZ=0
    g7: LineSegment [constr] StartX=-16 StartY=-13.5 StartZ=0 EndX=-10 EndY=-13.5 EndZ=0
    g8: LineSegment [constr] StartX=-10 StartY=-13.5 StartZ=0 EndX=-10 EndY=6.5 EndZ=0
    g9: LineSegment [constr] StartX=-10 StartY=6.5 StartZ=0 EndX=-16 EndY=6.5 EndZ=0
  constraints (27):
    c: Coincident(g0,g-4)
    c: Distance(g0,g-4) = 2
    c: Coincident(g1,g0)
    c: Diameter(g1) = 29
    c: Coincident(g2,g3)
    c: Coincident(g3,g4)
    c: Coincident(g4,g5)
    c: Coincident(g5,g2)
    c: Horizontal(g2)
    c: Horizontal(g4)
    c: Vertical(g3)
    c: Vertical(g5)
    c: Coincident(g2,g-5)
    c: Coincident(g6,g7)
    c: Coincident(g7,g8)
    c: Coincident(g8,g9)
    c: Coincident(g9,g6)
    c: Vertical(g6)
    c: Vertical(g8)
    c: Horizontal(g7)
    c: Horizontal(g9)
    c: Coincident(g6,g3)
    c: Horizontal(g2,g7)
    c: DistanceX(g4,g4) = 4
    c: DistanceX(g9,g9) = 6
    c: DistanceY(g5,g5) = 20
    c: Distance(g0,g8) = 2.8
FEATURE [PartDesign::Pad] Pad004  label="SwitchMountPad004"
  BaseFeature = -> Pad003
  Direction = (0,0,1)
  Length = 15
  Length2 = 10
  Profile = -> Sketch015
  ReferenceAxis = -> Sketch015 [N_Axis]
  Suppressed = false
  Type = 0
FEATURE [Sketcher::SketchObject] Sketch016
  ArcFitTolerance = 1e-06
  AttachmentSupport = -> [Pad004]
  ExternalGeometry = -> [Pad004]
  FullyConstrained = true
  MakeInternals = false
  MapMode = 5
  Placement = pos=(-20,0,0) rot=(0.57735,-0.57735,-0.57735;2.0944rad)
  sketch-geometry (2):
    g0: Circle CenterX=-1.5 CenterY=48 CenterZ=0 NormalX=0 NormalY=0 NormalZ=1 AngleXU=0 Radius=1.15
    g1: Circle CenterX=8 CenterY=48 CenterZ=0 NormalX=0 NormalY=0 NormalZ=1 AngleXU=0 Radius=1.15
  constraints (6):
    c: Equal(g1,g0)
    c: Horizontal(g0,g1)
    c: DistanceX(g0,g1) = 9.5
    c: Diameter(g1) = 2.3
    c: DistanceY(g0,g-3) = 7
    c: DistanceX(g-3,g0) = 5
FEATURE [PartDesign::Pocket] Pocket003  label="SwitchMountHolePocket003"
  BaseFeature = -> Pad004
  Direction = (1,0,0)
  Length = 5
  Length2 = 5
  Profile = -> Sketch016
  ReferenceAxis = -> Sketch016 [N_Axis]
  Suppressed = false
  Type = 1
FEATURE [Sketcher::SketchObject] Sketch017
  ArcFitTolerance = 1e-06
  AttachmentSupport = -> [Pocket003]
  ExternalGeometry = -> [Pocket003]
  FullyConstrained = true
  MakeInternals = false
  MapMode = 5
  Placement = pos=(0,0,40) rot=(0,0,1;0rad)
  sketch-geometry (4):
    g0: LineSegment StartX=11 StartY=22.5 StartZ=0 EndX=-11 EndY=22.5 EndZ=0
    g1: LineSegment StartX=11 StartY=22.5 StartZ=0 EndX=11 EndY=19.5 EndZ=0
    g2: LineSegment StartX=11 StartY=19.5 StartZ=0 EndX=-11 EndY=19.5 EndZ=0
    g3: LineSegment StartX=-11 StartY=19.5 StartZ=0 EndX=-11 EndY=22.5 EndZ=0
  constraints (10):
    c: Vertical(g1)
    c: Horizontal(g2)
    c: Coincident(g0,g-3)
    c: Coincident(g1,g0)
    c: DistanceY(g2,g0) = 3
    c: Coincident(g0,g-3)
    c: Coincident(g2,g1)
    c: Coincident(g3,g2)
    c: Coincident(g3,g0)
    c: Vertical(g3)
FEATURE [PartDesign::Pad] Pad005
  BaseFeature = -> Pocket003
  Direction = (0,0,1)
  Length = 12
  Length2 = 10
  Profile = -> Sketch017
  ReferenceAxis = -> Sketch017 [N_Axis]
  Suppressed = false
  Type = 0
FEATURE [Sketcher::SketchObject] Sketch018
  ArcFitTolerance = 1e-06
  AttachmentSupport = -> [XY_Plane006]
  FullyConstrained = true
  MakeInternals = false
  MapMode = 5
  sketch-geometry (2):
    g0: Circle CenterX=0 CenterY=0 CenterZ=0 NormalX=0 NormalY=0 NormalZ=1 AngleXU=0 Radius=7.2
    g1: Circle CenterX=0 CenterY=0 CenterZ=0 NormalX=0 NormalY=0 NormalZ=1 AngleXU=0 Radius=5.2
  constraints (4):
    c: Coincident(g0,g-1)
    c: Coincident(g1,g0)
    c: Diameter(g1) = 10.4
    c: Distance(g0,g1) = 2
FEATURE [PartDesign::Pad] Pad006
  Direction = (0,0,1)
  Length = 10
  Length2 = 10
  Midplane = true
  Profile = -> Sketch018
  ReferenceAxis = -> Sketch018 [N_Axis]
  Suppressed = false
  Type = 0
FEATURE [Sketcher::SketchObject] Sketch019
  ArcFitTolerance = 1e-06
  AttachmentSupport = -> [XZ_Plane006]
  FullyConstrained = true
  MakeInternals = false
  MapMode = 5
  Placement = pos=(0,0,0) rot=(1,0,0;1.5708rad)
  sketch-geometry (1):
    g0: Circle CenterX=0 CenterY=0 CenterZ=0 NormalX=0 NormalY=0 NormalZ=1 AngleXU=0 Radius=1.5
  constraints (2):
    c: Coincident(g0,g-1)
    c: Diameter(g0) = 3
FEATURE [PartDesign::Pocket] Pocket004
  BaseFeature = -> Pad006
  Direction = (0,1,-2e-16)
  Length = 5
  Length2 = 5
  Midplane = true
  Profile = -> Sketch019
  ReferenceAxis = -> Sketch019 [N_Axis]
  Suppressed = false
  Type = 1
FEATURE [PartDesign::Body] Body006  label="SlidingStop"
  AllowCompound = false
  Group = -> [Sketch018,Pad006,Sketch019,Pocket004]
  Origin = -> Origin006
  Tip = -> Pocket004
FEATURE [Sketcher::SketchObject] Sketch020
  ArcFitTolerance = 1e-06
  AttachmentSupport = -> [XZ_Plane007]
  FullyConstrained = true
  MakeInternals = false
  MapMode = 5
  Placement = pos=(0,0,0) rot=(1,0,0;1.5708rad)
  sketch-geometry (6):
    g0: LineSegment StartX=-14.5 StartY=0 StartZ=0 EndX=-14.5 EndY=3 EndZ=0
    g1: LineSegment StartX=-14.5 StartY=3 StartZ=0 EndX=-8.2 EndY=3 EndZ=0
    g2: LineSegment StartX=-8.2 StartY=3 StartZ=0 EndX=-8.2 EndY=11 EndZ=0
    g3: LineSegment StartX=-8.2 StartY=11 StartZ=0 EndX=-5.2 EndY=11 EndZ=0
    g4: LineSegment StartX=-5.2 StartY=11 StartZ=0 EndX=-5.2 EndY=0 EndZ=0
    g5: LineSegment StartX=-5.2 StartY=0 StartZ=0 EndX=-14.5 EndY=0 EndZ=0
  constraints (18):
    c: PointOnObject(g0,g-1)
    c: Vertical(g0)
    c: Coincident(g0,g1)
    c: Horizontal(g1)
    c: Coincident(g1,g2)
    c: Vertical(g2)
    c: Coincident(g2,g3)
    c: Horizontal(g3)
    c: Coincident(g3,g4)
    c: PointOnObject(g4,g-1)
    c: Vertical(g4)
    c: Coincident(g4,g5)
    c: Coincident(g5,g0)
    c: DistanceX(g4,g-1) = 5.2
    c: DistanceX(g3,g3) = 3
    c: DistanceX(g0,g-1) = 14.5
    c: DistanceY(g0,g0) = 3
    c: DistanceY(g2,g2) = 8
FEATURE [PartDesign::Revolution] Revolution004
  Angle = 360
  Angle2 = 60
  Axis = (0,2e-16,1)
  Base = (0,0,0)
  Placement = pos=(0,0,0) rot=(1,0,0;1.5708rad)
  Profile = -> Sketch020
  ReferenceAxis = -> Sketch020 [V_Axis]
  Suppressed = false
  Type = 0
FEATURE [Sketcher::SketchObject] Sketch021
  ArcFitTolerance = 1e-06
  AttachmentSupport = -> [XZ_Plane007]
  ExternalGeometry = -> [Revolution004]
  FullyConstrained = true
  MakeInternals = false
  MapMode = 5
  Placement = pos=(0,0,0) rot=(1,0,0;1.5708rad)
  sketch-geometry (2):
    g0: LineSegment [constr] StartX=-8.2 StartY=7 StartZ=0 EndX=0 EndY=7 EndZ=0
    g1: Circle CenterX=0 CenterY=7 CenterZ=0 NormalX=0 NormalY=0 NormalZ=1 AngleXU=0 Radius=1.5
  constraints (5):
    c: Symmetric(g-3,g-3,g0)
    c: PointOnObject(g0,g-2)
    c: Horizontal(g0)
    c: Coincident(g1,g0)
    c: Diameter(g1) = 3
FEATURE [PartDesign::Pocket] Pocket005
  BaseFeature = -> Revolution004
  Direction = (0,1,-2e-16)
  Length = 5
  Length2 = 5
  Midplane = true
  Placement = pos=(0,0,0) rot=(1,0,0;1.5708rad)
  Profile = -> Sketch021
  ReferenceAxis = -> Sketch021 [N_Axis]
  Suppressed = false
  Type = 1
FEATURE [PartDesign::Body] Body007  label="SwitchActuator"
  AllowCompound = false
  Group = -> [Sketch020,Revolution004,Sketch021,Pocket005]
  Origin = -> Origin007
  Tip = -> Pocket005
FEATURE [Sketcher::SketchObject] Sketch022
  ArcFitTolerance = 1e-06
  AttachmentSupport = -> [XZ_Plane005]
  ExternalGeometry = -> [Pad005]
  FullyConstrained = true
  MakeInternals = false
  MapMode = 5
  Placement = pos=(0,0,0) rot=(1,0,0;1.5708rad)
  sketch-geometry (2):
    g0: Circle CenterX=5 CenterY=47 CenterZ=0 NormalX=0 NormalY=0 NormalZ=1 AngleXU=0 Radius=3
    g1: Circle CenterX=-5 CenterY=47 CenterZ=0 NormalX=0 NormalY=0 NormalZ=1 AngleXU=0 Radius=3
  constraints (5):
    c: Diameter(g0) = 6
    c: DistanceY(g-3,g0) = 7
    c: Equal(g1,g0)
    c: Symmetric(g1,g0,g-2)
    c: DistanceX(g1,g0) = 10
FEATURE [PartDesign::Pocket] Pocket006
  BaseFeature = -> Pad005
  Direction = (0,1,-2e-16)
  Length = 5
  Length2 = 5
  Midplane = true
  Profile = -> Sketch022
  ReferenceAxis = -> Sketch022 [N_Axis]
  Suppressed = false
  Type = 1
FEATURE [PartDesign::Fillet] Fillet003
  Base = -> Pocket006 [Edge60]
  BaseFeature = -> Pocket006
  Radius = 3.5
  SupportTransform = false
  Suppressed = false
  UseAllEdges = false
FEATURE [PartDesign::Fillet] Fillet004
  Base = -> Fillet003 [Edge34,Edge23,Edge59,Edge105,Edge15]
  BaseFeature = -> Fillet003
  Radius = 4
  SupportTransform = false
  Suppressed = false
  UseAllEdges = false
FEATURE [PartDesign::Body] Body005  label="DEPRECATEDSlidingBodyFull"
  AllowCompound = false
  Group = -> [Sketch013,Pad002,Fillet002,Sketch014,Pad003,Sketch015,Pad004,Sketch016,Pocket003,Sketch017,Pad005,Sketch022,Pocket006,Fillet003,Fillet004]
  Origin = -> Origin005
  Tip = -> Fillet004
FEATURE [Sketcher::SketchObject] Sketch023
  ArcFitTolerance = 1e-06
  AttachmentSupport = -> [XY_Plane008]
  FullyConstrained = true
  MakeInternals = false
  MapMode = 5
  sketch-geometry (17):
    g0: LineSegment StartX=-20 StartY=22.5 StartZ=0 EndX=-20 EndY=-22.5 EndZ=0
    g1: LineSegment StartX=-20 StartY=-22.5 StartZ=0 EndX=20 EndY=-22.5 EndZ=0
    g2: LineSegment StartX=20 StartY=-22.5 StartZ=0 EndX=20 EndY=22.5 EndZ=0
    g3: LineSegment StartX=20 StartY=22.5 StartZ=0 EndX=-20 EndY=22.5 EndZ=0
    g4: LineSegment [constr] StartX=-16 StartY=18.5 StartZ=0 EndX=-16 EndY=-18.5 EndZ=0
    g5: LineSegment [constr] StartX=-16 StartY=-18.5 StartZ=0 EndX=16 EndY=-18.5 EndZ=0
    g6: LineSegment [constr] StartX=16 StartY=-18.5 StartZ=0 EndX=16 EndY=18.5 EndZ=0
    g7: LineSegment [constr] StartX=16 StartY=18.5 StartZ=0 EndX=-16 EndY=18.5 EndZ=0
    g8: Circle CenterX=-16 CenterY=18.5 CenterZ=0 NormalX=0 NormalY=0 NormalZ=1 AngleXU=0 Radius=1.75
    g9: Circle CenterX=16 CenterY=18.5 CenterZ=0 NormalX=0 NormalY=0 NormalZ=1 AngleXU=0 Radius=1.75
    g10: Circle CenterX=16 CenterY=-18.5 CenterZ=0 NormalX=0 NormalY=0 NormalZ=1 AngleXU=0 Radius=1.75
    g11: Circle CenterX=-16 CenterY=-18.5 CenterZ=0 NormalX=0 NormalY=0 NormalZ=1 AngleXU=0 Radius=1.75
    g12: Circle CenterX=0 CenterY=-9.5 CenterZ=0 NormalX=0 NormalY=0 NormalZ=1 AngleXU=0 Radius=5.15
    g13: Circle CenterX=0 CenterY=-19 CenterZ=0 NormalX=0 NormalY=0 NormalZ=1 AngleXU=0 Radius=1.6
    g14: Circle [constr] CenterX=0 CenterY=-19 CenterZ=0 NormalX=0 NormalY=0 NormalZ=1 AngleXU=0 Radius=3.5
    g15: Circle CenterX=-10 CenterY=10.5 CenterZ=0 NormalX=0 NormalY=0 NormalZ=1 AngleXU=0 Radius=1.6
    g16: Circle CenterX=10 CenterY=10.5 CenterZ=0 NormalX=0 NormalY=0 NormalZ=1 AngleXU=0 Radius=1.6
  constraints (43):
    c: Coincident(g0,g1)
    c: Coincident(g1,g2)
    c: Coincident(g2,g3)
    c: Coincident(g3,g0)
    c: Vertical(g0)
    c: Vertical(g2)
    c: Horizontal(g1)
    c: Horizontal(g3)
    c: Symmetric(g0,g1,g-1)
    c: Coincident(g4,g5)
    c: Coincident(g5,g6)
    c: Coincident(g6,g7)
    c: Coincident(g7,g4)
    c: Vertical(g4)
    c: Vertical(g6)
    c: Horizontal(g5)
    c: Horizontal(g7)
    c: DistanceX(g0,g4) = 4
    c: DistanceY(g4,g0) = 4
    c: Coincident(g8,g4)
    c: Coincident(g9,g6)
    c: Coincident(g10,g5)
    c: Coincident(g11,g4)
    c: Equal(g8,g9)
    c: Equal(g9,g10)
    c: Equal(g10,g11)
    c: Diameter(g8) = 3.5
    c: PointOnObject(g12,g-2)
    c: Diameter(g12) = 10.3
    c: Symmetric(g5,g4,g-1)
    c: DistanceY(g2,g2) = 45
    c: DistanceX(g3,g3) = 40
    c: DistanceY(g1,g12) = 13
    c: PointOnObject(g13,g-2)
    c: Diameter(g13) = 3.2
    c: Coincident(g14,g13)
    c: Diameter(g14) = 7
    c: Tangent(g14,g1)
    c: Equal(g16,g15)
    c: Equal(g15,g13)
    c: DistanceY(g16,g6) = 8
    c: Symmetric(g16,g15,g-2)
    c: DistanceX(g15,g16) = 20
FEATURE [PartDesign::Pad] Pad007  label="FrontPad003"
  Direction = (0,0,1)
  Length = 4
  Length2 = 10
  Profile = -> Sketch023
  ReferenceAxis = -> Sketch023 [N_Axis]
  Suppressed = false
  Type = 0
FEATURE [PartDesign::Fillet] Fillet005
  Base = -> Pad007 [Edge8,Edge2,Edge1,Edge5]
  BaseFeature = -> Pad007
  Radius = 3
  SupportTransform = false
  Suppressed = false
  UseAllEdges = false
FEATURE [Sketcher::SketchObject] Sketch029
  ArcFitTolerance = 1e-06
  AttachmentSupport = -> [XY_Plane009]
  FullyConstrained = true
  MakeInternals = false
  MapMode = 5
  sketch-geometry (25):
    g0: LineSegment StartX=-20 StartY=13.5 StartZ=0 EndX=-20 EndY=-13.5 EndZ=0
    g1: LineSegment StartX=-11 StartY=-22.5 StartZ=0 EndX=11 EndY=-22.5 EndZ=0
    g2: LineSegment StartX=11 StartY=22.5 StartZ=0 EndX=-11 EndY=22.5 EndZ=0
    g3: LineSegment [constr] StartX=-16 StartY=18.5 StartZ=0 EndX=-16 EndY=-18.5 EndZ=0
    g4: LineSegment [constr] StartX=-16 StartY=-18.5 StartZ=0 EndX=16 EndY=-18.5 EndZ=0
    g5: LineSegment [constr] StartX=16 StartY=-18.5 StartZ=0 EndX=16 EndY=18.5 EndZ=0
    g6: LineSegment [constr] StartX=16 StartY=18.5 StartZ=0 EndX=-16 EndY=18.5 EndZ=0
    g7: Circle CenterX=0 CenterY=-9.5 CenterZ=0 NormalX=0 NormalY=0 NormalZ=1 AngleXU=0 Radius=5.15
    g8: Circle CenterX=0 CenterY=-19 CenterZ=0 NormalX=0 NormalY=0 NormalZ=1 AngleXU=0 Radius=1.6
    g9: Circle [constr] CenterX=0 CenterY=-19 CenterZ=0 NormalX=0 NormalY=0 NormalZ=1 AngleXU=0 Radius=3.5
    g10: Circle CenterX=-10 CenterY=10.5 CenterZ=0 NormalX=0 NormalY=0 NormalZ=1 AngleXU=0 Radius=1.6
    g11: Circle CenterX=10 CenterY=10.5 CenterZ=0 NormalX=0 NormalY=0 NormalZ=1 AngleXU=0 Radius=1.6
    g12: ArcOfCircle CenterX=-16 CenterY=-18.5 CenterZ=0 NormalX=0 NormalY=0 NormalZ=1 AngleXU=0 Radius=5 StartAngle=4e-16 EndAngle=1.5708
    g13: LineSegment StartX=-11 StartY=-18.5 StartZ=0 EndX=-11 EndY=-22.5 EndZ=0
    g14: LineSegment StartX=-16 StartY=-13.5 StartZ=0 EndX=-20 EndY=-13.5 EndZ=0
    g15: LineSegment StartX=11 StartY=-22.5 StartZ=0 EndX=11 EndY=-18.5 EndZ=0
    g16: ArcOfCircle CenterX=16 CenterY=-18.5 CenterZ=0 NormalX=0 NormalY=0 NormalZ=1 AngleXU=0 Radius=5 StartAngle=1.5708 EndAngle=3.14159
    g17: LineSegment StartX=16 StartY=-13.5 StartZ=0 EndX=20 EndY=-13.5 EndZ=0
    g18: ArcOfCircle CenterX=16 CenterY=18.5 CenterZ=0 NormalX=0 NormalY=0 NormalZ=1 AngleXU=0 Radius=5 StartAngle=3.14159 EndAngle=4.71239
    g19: ArcOfCircle CenterX=-16 CenterY=18.5 CenterZ=0 NormalX=0 NormalY=0 NormalZ=1 AngleXU=0 Radius=5 StartAngle=4.71239 EndAngle=6.28319
    g20: LineSegment StartX=-11 StartY=18.5 StartZ=0 EndX=-11 EndY=22.5 EndZ=0
    g21: LineSegment StartX=-16 StartY=13.5 StartZ=0 EndX=-20 EndY=13.5 EndZ=0
    g22: LineSegment StartX=11 StartY=18.5 StartZ=0 EndX=11 EndY=22.5 EndZ=0
    g23: LineSegment StartX=16 StartY=13.5 StartZ=0 EndX=20 EndY=13.5 EndZ=0
    g24: LineSegment StartX=20 StartY=13.5 StartZ=0 EndX=20 EndY=-13.5 EndZ=0
  constraints (68):
    c: Vertical(g0)
    c: Horizontal(g1)
    c: Horizontal(g2)
    c: Coincident(g3,g4)
    c: Coincident(g4,g5)
    c: Coincident(g5,g6)
    c: Coincident(g6,g3)
    c: Vertical(g3)
    c: Vertical(g5)
    c: Horizontal(g4)
    c: Horizontal(g6)
    c: PointOnObject(g7,g-2)
    c: Diameter(g7) = 10.3
    c: Symmetric(g4,g3,g-1)
    c: PointOnObject(g8,g-2)
    c: Diameter(g8) = 3.2
    c: Coincident(g9,g8)
    c: Diameter(g9) = 7
    c: Tangent(g9,g1)
    c: Equal(g11,g10)
    c: Equal(g10,g8)
    c: DistanceY(g11,g5) = 8
    c: Symmetric(g11,g10,g-2)
    c: DistanceX(g10,g11) = 20
    c: Coincident(g12,g3)
    c: PointOnObject(g12,g3)
    c: PointOnObject(g12,g4)
    c: Coincident(g13,g12)
    c: Vertical(g13)
    c: Coincident(g14,g12)
    c: Horizontal(g14)
    c: Radius(g12) = 5
    c: PointOnObject(g15,g4)
    c: Tangent(g15,g16) = 1.5708
    c: PointOnObject(g16,g5)
    c: Tangent(g16,g17) = 1.5708
    c: Coincident(g4,g16)
    c: Coincident(g18,g5)
    c: PointOnObject(g18,g5)
    c: PointOnObject(g18,g6)
    c: Coincident(g19,g3)
    c: PointOnObject(g19,g3)
    c: PointOnObject(g19,g6)
    c: Coincident(g20,g19)
    c: Vertical(g20)
    c: Coincident(g21,g19)
    c: Horizontal(g21)
    c: Coincident(g22,g18)
    c: Vertical(g22)
    c: Coincident(g23,g18)
    c: Horizontal(g23)
    c: Equal(g16,g19)
    c: Coincident(g2,g20)
    c: Coincident(g0,g21)
    c: Coincident(g2,g22)
    c: Coincident(g1,g15)
    c: Coincident(g1,g13)
    c: Coincident(g0,g14)
    c: DistanceX(g1,g1) = 22
    c: DistanceY(g0,g0) = 27
    c: Coincident(g24,g23)
    c: Coincident(g24,g17)
    c: Vertical(g24)
    c: DistanceX(g0,g17) = 40
    c: DistanceY(g1,g2) = 45
    c: Symmetric(g23,g0,g-2)
    c: Symmetric(g2,g1,g-1)
    c: DistanceY(g4,g7) = 9
FEATURE [PartDesign::Pad] Pad011  label="FrontPad004"
  Direction = (0,0,1)
  Length = 4
  Length2 = 10
  Profile = -> Sketch029
  ReferenceAxis = -> Sketch029 [N_Axis]
  Reversed = true
  Suppressed = false
  Type = 0
FEATURE [Sketcher::SketchObject] Sketch030
  ArcFitTolerance = 1e-06
  ExternalGeometry = -> [Pad011]
  FullyConstrained = false
  MakeInternals = false
  MapMode = 5
  sketch-geometry (9):
    g0: Circle [constr] CenterX=0 CenterY=-9.5 CenterZ=0 NormalX=0 NormalY=0 NormalZ=1 AngleXU=0 Radius=14.5
    g1: LineSegment StartX=-20 StartY=-13.5 StartZ=0 EndX=-16 EndY=-13.5 EndZ=0
    g2: LineSegment StartX=-16 StartY=-13.5 StartZ=0 EndX=-16 EndY=6.5 EndZ=0
    g3: LineSegment StartX=-16 StartY=6.5 StartZ=0 EndX=-20 EndY=6.5 EndZ=0
    g4: LineSegment StartX=-20 StartY=6.5 StartZ=0 EndX=-20 EndY=-13.5 EndZ=0
    g5: LineSegment [constr] StartX=-16 StartY=6.5 StartZ=0 EndX=-16 EndY=-13.5 EndZ=0
    g6: LineSegment [constr] StartX=-16 StartY=-13.5 StartZ=0 EndX=-10 EndY=-13.5 EndZ=0
    g7: LineSegment [constr] StartX=-10 StartY=-13.5 StartZ=0 EndX=-10 EndY=6.5 EndZ=0
    g8: LineSegment [constr] StartX=-10 StartY=6.5 StartZ=0 EndX=-16 EndY=6.5 EndZ=0
  constraints (23):
    c: Diameter(g0) = 29
    c: Coincident(g1,g2)
    c: Coincident(g2,g3)
    c: Coincident(g3,g4)
    c: Coincident(g4,g1)
    c: Horizontal(g1)
    c: Horizontal(g3)
    c: Vertical(g2)
    c: Vertical(g4)
    c: Coincident(g1,g-4)
    c: Coincident(g5,g6)
    c: Coincident(g6,g7)
    c: Coincident(g7,g8)
    c: Coincident(g8,g5)
    c: Vertical(g5)
    c: Vertical(g7)
    c: Horizontal(g6)
    c: Horizontal(g8)
    c: Coincident(g5,g2)
    c: Horizontal(g1,g6)
    c: DistanceX(g3,g3) = 4
    c: DistanceX(g8,g8) = 6
    c: DistanceY(g4,g4) = 20
FEATURE [PartDesign::Pad] Pad012  label="SwitchMountPad006"
  BaseFeature = -> Pad011
  Direction = (0,0,1)
  Length = 15
  Length2 = 10
  Profile = -> Sketch030
  ReferenceAxis = -> Sketch030 [N_Axis]
  Suppressed = false
  Type = 0
FEATURE [Sketcher::SketchObject] Sketch031
  ArcFitTolerance = 1e-06
  AttachmentSupport = -> [Pad012]
  ExternalGeometry = -> [Pad012]
  FullyConstrained = true
  MakeInternals = false
  MapMode = 5
  Placement = pos=(-16,0,0) rot=(0.57735,0.57735,0.57735;2.0944rad)
  sketch-geometry (2):
    g0: Circle CenterX=-8.5 CenterY=8 CenterZ=0 NormalX=0 NormalY=0 NormalZ=1 AngleXU=0 Radius=1.15
    g1: Circle CenterX=1 CenterY=8 CenterZ=0 NormalX=0 NormalY=0 NormalZ=1 AngleXU=0 Radius=1.15
  constraints (6):
    c: Equal(g1,g0)
    c: Horizontal(g0,g1)
    c: DistanceX(g0,g1) = 9.5
    c: Diameter(g1) = 2.3
    c: DistanceX(g-3,g0) = 5
    c: DistanceY(g0,g-3) = 7
FEATURE [Sketcher::SketchObject] Sketch034
  ArcFitTolerance = 1e-06
  AttachmentSupport = -> [XY_Plane008]
  ExternalGeometry = -> [Pad007]
  FullyConstrained = true
  MakeInternals = false
  MapMode = 5
  sketch-geometry (3):
    g0: Circle CenterX=0 CenterY=-19 CenterZ=0 NormalX=0 NormalY=0 NormalZ=1 AngleXU=0 Radius=1.6
    g1: Circle CenterX=10 CenterY=10.5 CenterZ=0 NormalX=0 NormalY=0 NormalZ=1 AngleXU=0 Radius=1.6
    g2: Circle CenterX=-10 CenterY=10.5 CenterZ=0 NormalX=0 NormalY=0 NormalZ=1 AngleXU=0 Radius=1.6
  constraints (6):
    c: Coincident(g0,g-5)
    c: Equal(g0,g-5)
    c: Coincident(g1,g-4)
    c: Equal(g1,g-4)
    c: Coincident(g2,g-3)
    c: Equal(g2,g-3)
FEATURE [PartDesign::Hole] Hole001
  BaseFeature = -> Fillet005
  CustomThreadClearance = 0
  Depth = 25
  DepthType = 0
  Diameter = 3.4
  DrillForDepth = false
  DrillPoint = 1
  DrillPointAngle = 118
  HoleCutCountersinkAngle = 90
  HoleCutCustomValues = false
  HoleCutDepth = 0
  HoleCutDiameter = 6.2
  HoleCutType = 2
  ModelThread = false
  Profile = -> Sketch034
  Reversed = true
  Suppressed = false
  Tapered = false
  TaperedAngle = 90
  ThreadClass = 0
  ThreadDepth = 25
  ThreadDepthType = 0
  ThreadDirection = 0
  ThreadFit = 0
  ThreadSize = 9
  ThreadType = 1
  Threaded = false
  UseCustomThreadClearance = false
FEATURE [PartDesign::Body] Body008  label="SlidingBodyTop"
  AllowCompound = false
  Group = -> [Sketch023,Pad007,Fillet005,Sketch034,Hole001]
  Origin = -> Origin008
  Tip = -> Hole001
FEATURE [PartDesign::Pocket] Pocket011
  BaseFeature = -> Pad012
  Direction = (-1,0,0)
  Length = 5
  Length2 = 5
  Midplane = true
  Profile = -> Sketch031
  ReferenceAxis = -> Sketch031 [N_Axis]
  Suppressed = false
  Type = 1
FEATURE [Sketcher::SketchObject] Sketch035
  ArcFitTolerance = 1e-06
  AttachmentSupport = -> [Pocket011]
  ExternalGeometry = -> [Pocket011]
  FullyConstrained = true
  MakeInternals = false
  MapMode = 5
  sketch-geometry (4):
    g0: LineSegment StartX=-11 StartY=22.5 StartZ=0 EndX=-11 EndY=19.5 EndZ=0
    g1: LineSegment StartX=-11 StartY=19.5 StartZ=0 EndX=11 EndY=19.5 EndZ=0
    g2: LineSegment StartX=11 StartY=19.5 StartZ=0 EndX=11 EndY=22.5 EndZ=0
    g3: LineSegment StartX=11 StartY=22.5 StartZ=0 EndX=-11 EndY=22.5 EndZ=0
  constraints (10):
    c: Coincident(g0,g1)
    c: Coincident(g1,g2)
    c: Coincident(g2,g3)
    c: Coincident(g3,g0)
    c: Vertical(g0)
    c: Vertical(g2)
    c: Horizontal(g1)
    c: Coincident(g0,g-3)
    c: Coincident(g2,g-3)
    c: DistanceY(g0,g0) = 3
FEATURE [PartDesign::Pad] Pad013
  BaseFeature = -> Pocket011
  Direction = (0,0,1)
  Length = 12
  Length2 = 10
  Profile = -> Sketch035
  ReferenceAxis = -> Sketch035 [N_Axis]
  Suppressed = false
  Type = 0
FEATURE [Sketcher::SketchObject] Sketch036
  ArcFitTolerance = 1e-06
  AttachmentSupport = -> [XZ_Plane009]
  ExternalGeometry = -> [Pad013]
  FullyConstrained = true
  MakeInternals = false
  MapMode = 5
  Placement = pos=(0,0,0) rot=(1,0,0;1.5708rad)
  sketch-geometry (2):
    g0: Circle CenterX=-5 CenterY=6 CenterZ=0 NormalX=0 NormalY=0 NormalZ=1 AngleXU=0 Radius=2.5
    g1: Circle CenterX=5 CenterY=6 CenterZ=0 NormalX=0 NormalY=0 NormalZ=1 AngleXU=0 Radius=2.5
  constraints (5):
    c: Diameter(g1) = 5
    c: Equal(g1,g0)
    c: Symmetric(g1,g0,g-2)
    c: DistanceY(g0,g-3) = 6
    c: DistanceX(g0,g1) = 10
FEATURE [PartDesign::Pocket] Pocket012
  BaseFeature = -> Pad013
  Direction = (0,1,-2e-16)
  Length = 5
  Length2 = 5
  Profile = -> Sketch036
  ReferenceAxis = -> Sketch036 [N_Axis]
  Suppressed = false
  Type = 1
FEATURE [PartDesign::Fillet] Fillet006
  Base = -> Pocket012 [Edge85,Edge77,Edge84,Edge88]
  BaseFeature = -> Pocket012
  Radius = 3
  SupportTransform = false
  Suppressed = false
  UseAllEdges = false
FEATURE [PartDesign::Fillet] Fillet007
  Base = -> Fillet006 [Edge31,Edge11]
  BaseFeature = -> Fillet006
  Radius = 3
  SupportTransform = false
  Suppressed = false
  UseAllEdges = false
FEATURE [PartDesign::Body] Body009  label="SlidingBodyBottom"
  AllowCompound = false
  Group = -> [Sketch029,Pad011,Sketch030,Pad012,Sketch031,Pocket011,Sketch035,Pad013,Sketch036,Pocket012,Fillet006,Fillet007]
  Origin = -> Origin009
  Tip = -> Fillet007
FEATURE [Part::Part2DObjectPython] Clone2D  label="Sketch029 (2D)"  # Draft 2D object (typed FeaturePython)
  Fuse = false
  Objects = -> [Sketch029]
  Scale = (1,1,1)
FEATURE [Sketcher::SketchObject] Sketch037
  ArcFitTolerance = 1e-06
  AttachmentSupport = -> [XY_Plane010]
  ExternalGeometry = -> [Clone2D]
  FullyConstrained = true
  MakeInternals = false
  MapMode = 5
  sketch-geometry (14):
    g0: ArcOfCircle CenterX=-16 CenterY=18.5 CenterZ=0 NormalX=0 NormalY=0 NormalZ=1 AngleXU=0 Radius=5 StartAngle=4.71239 EndAngle=6.28319
    g1: ArcOfCircle CenterX=16 CenterY=18.5 CenterZ=0 NormalX=0 NormalY=0 NormalZ=1 AngleXU=0 Radius=5 StartAngle=3.14159 EndAngle=4.71239
    g2: ArcOfCircle CenterX=16 CenterY=-18.5 CenterZ=0 NormalX=0 NormalY=0 NormalZ=1 AngleXU=0 Radius=5 StartAngle=1.5708 EndAngle=3.14159
    g3: ArcOfCircle CenterX=-16 CenterY=-18.5 CenterZ=0 NormalX=0 NormalY=0 NormalZ=1 AngleXU=0 Radius=5 StartAngle=8e-16 EndAngle=1.5708
    g4: LineSegment StartX=-16 StartY=13.5 StartZ=0 EndX=-16 EndY=-13.5 EndZ=0
    g5: LineSegment StartX=16 StartY=-13.5 StartZ=0 EndX=16 EndY=13.5 EndZ=0
    g6: LineSegment StartX=-11 StartY=18.5 StartZ=0 EndX=11 EndY=18.5 EndZ=0
    g7: LineSegment StartX=-11 StartY=-18.5 StartZ=0 EndX=-11 EndY=-22.5 EndZ=0
    g8: LineSegment StartX=-11 StartY=-22.5 StartZ=0 EndX=11 EndY=-22.5 EndZ=0
    g9: LineSegment StartX=11 StartY=-22.5 StartZ=0 EndX=11 EndY=-18.5 EndZ=0
    g10: Circle CenterX=-10 CenterY=10.5 CenterZ=0 NormalX=0 NormalY=0 NormalZ=1 AngleXU=0 Radius=1.6
    g11: Circle CenterX=10 CenterY=10.5 CenterZ=0 NormalX=0 NormalY=0 NormalZ=1 AngleXU=0 Radius=1.6
    g12: Circle CenterX=0 CenterY=-9.5 CenterZ=0 NormalX=0 NormalY=0 NormalZ=1 AngleXU=0 Radius=5.65
    g13: Circle CenterX=0 CenterY=-19 CenterZ=0 NormalX=0 NormalY=0 NormalZ=1 AngleXU=0 Radius=1.6
  constraints (32):
    c: Coincident(g0,g-3)
    c: Coincident(g0,g-3)
    c: Coincident(g1,g-10)
    c: Coincident(g1,g-10)
    c: Coincident(g1,g-10)
    c: Coincident(g2,g-9)
    c: Coincident(g2,g-9)
    c: Coincident(g3,g-8)
    c: Coincident(g3,g-8)
    c: Vertical(g3,g0)
    c: Horizontal(g0,g0)
    c: Horizontal(g2,g2)
    c: Coincident(g4,g0)
    c: Coincident(g4,g3)
    c: Coincident(g5,g2)
    c: Coincident(g5,g1)
    c: Coincident(g6,g0)
    c: Coincident(g6,g1)
    c: Tangent(g3,g7) = 1.5708
    c: Coincident(g7,g8)
    c: Coincident(g8,g-11)
    c: Horizontal(g8)
    c: Coincident(g8,g9)
    c: Coincident(g9,g2)
    c: Coincident(g10,g-4)
    c: Coincident(g11,g-5)
    c: Coincident(g12,g-7)
    c: Coincident(g13,g-6)
    c: Equal(g13,g11)
    c: Equal(g11,g10)
    c: Equal(g10,g-4)
    c: Distance(g12,g-7) = 0.5
FEATURE [PartDesign::Pad] Pad014  label="BasePad014"
  Direction = (0,0,1)
  Length = 2
  Length2 = 10
  Profile = -> Sketch037
  ReferenceAxis = -> Sketch037 [N_Axis]
  Reversed = true
  Suppressed = false
  Type = 0
FEATURE [Sketcher::SketchObject] Sketch038
  ArcFitTolerance = 1e-06
  AttachmentSupport = -> [XY_Plane010]
  ExternalGeometry = -> [Clone2D]
  FullyConstrained = true
  MakeInternals = false
  MapMode = 5
  sketch-geometry (11):
    g0: ArcOfCircle CenterX=0 CenterY=-9.5 CenterZ=0 NormalX=0 NormalY=0 NormalZ=1 AngleXU=0 Radius=5.15 StartAngle=3.33701 EndAngle=6.08777
    g1: LineSegment StartX=5.05198 StartY=-10.5 StartZ=0 EndX=11 EndY=-10.5 EndZ=0
    g2: LineSegment StartX=11 StartY=-10.5 StartZ=0 EndX=11 EndY=-22.5 EndZ=0
    g3: LineSegment StartX=11 StartY=-22.5 StartZ=0 EndX=-11 EndY=-22.5 EndZ=0
    g4: LineSegment StartX=-11 StartY=-22.5 StartZ=0 EndX=-11 EndY=-10.5 EndZ=0
    g5: LineSegment StartX=-11 StartY=-10.5 StartZ=0 EndX=-5.05198 EndY=-10.5 EndZ=0
    g6: Circle CenterX=0 CenterY=-19 CenterZ=0 NormalX=0 NormalY=0 NormalZ=1 AngleXU=0 Radius=1.6
    g7: Circle CenterX=-10 CenterY=10.5 CenterZ=0 NormalX=0 NormalY=0 NormalZ=1 AngleXU=0 Radius=1.6
    g8: Circle CenterX=10 CenterY=10.5 CenterZ=0 NormalX=0 NormalY=0 NormalZ=1 AngleXU=0 Radius=1.6
    g9: Circle CenterX=-10 CenterY=10.5 CenterZ=0 NormalX=0 NormalY=0 NormalZ=1 AngleXU=0 Radius=4.1
    g10: Circle CenterX=10 CenterY=10.5 CenterZ=0 NormalX=0 NormalY=0 NormalZ=1 AngleXU=0 Radius=4.1
  constraints (26):
    c: Coincident(g0,g-3)
    c: Equal(g0,g-3)
    c: Horizontal(g0,g0)
    c: DistanceY(g0,g0) = 1
    c: Coincident(g0,g1)
    c: Horizontal(g1)
    c: Coincident(g1,g2)
    c: Coincident(g2,g-4)
    c: Vertical(g2)
    c: Coincident(g2,g3)
    c: Coincident(g3,g-4)
    c: Coincident(g3,g4)
    c: Vertical(g4)
    c: Coincident(g4,g5)
    c: Coincident(g5,g0)
    c: Horizontal(g5)
    c: Coincident(g6,g-5)
    c: Equal(g6,g-5)
    c: Coincident(g7,g-6)
    c: Coincident(g8,g-7)
    c: Equal(g8,g7)
    c: Equal(g7,g6)
    c: Coincident(g9,g7)
    c: Coincident(g10,g8)
    c: Equal(g10,g9)
    c: Distance(g9,g7) = 2.5
FEATURE [PartDesign::Pad] Pad015  label="BrakeMainPad015"
  BaseFeature = -> Pad014
  Direction = (0,0,1)
  Length = 10
  Length2 = 10
  Profile = -> Sketch038
  ReferenceAxis = -> Sketch038 [N_Axis]
  Suppressed = false
  Type = 0
FEATURE [Sketcher::SketchObject] Sketch039
  ArcFitTolerance = 1e-06
  AttachmentSupport = -> [XZ_Plane010]
  ExternalGeometry = -> [Pad015]
  FullyConstrained = true
  MakeInternals = false
  MapMode = 5
  Placement = pos=(0,0,0) rot=(1,0,0;1.5708rad)
  sketch-geometry (5):
    g0: Circle CenterX=-8.02599 CenterY=5 CenterZ=0 NormalX=0 NormalY=0 NormalZ=1 AngleXU=0 Radius=1.65
    g1: Circle CenterX=8.02599 CenterY=5 CenterZ=0 NormalX=0 NormalY=0 NormalZ=1 AngleXU=0 Radius=1.65
    g2: LineSegment [constr] StartX=-11 StartY=5 StartZ=0 EndX=-5.05198 EndY=5 EndZ=0
    g3: LineSegment [constr] StartX=-11 StartY=10 StartZ=0 EndX=-5.05198 EndY=10 EndZ=0
    g4: LineSegment [constr] StartX=-8.02599 StartY=10 StartZ=0 EndX=-8.02599 EndY=5 EndZ=0
  constraints (11):
    c: Symmetric(g1,g0,g-2)
    c: Symmetric(g-3,g-3,g2)
    c: Symmetric(g-4,g-4,g2)
    c: PointOnObject(g0,g2)
    c: Coincident(g3,g-3)
    c: Coincident(g3,g-4)
    c: Symmetric(g3,g3,g4)
    c: Coincident(g4,g0)
    c: Vertical(g4)
    c: Equal(g0,g1)
    c: Diameter(g0) = 3.3
FEATURE [PartDesign::Pocket] Pocket013
  BaseFeature = -> Pad015
  Direction = (0,1,-2e-16)
  Length = 5
  Length2 = 5
  Profile = -> Sketch039
  ReferenceAxis = -> Sketch039 [N_Axis]
  Reversed = true
  Suppressed = false
  Type = 1
FEATURE [PartDesign::Body] Body010  label="SlidingBodyBrakeBase"
  AllowCompound = false
  Group = -> [Clone2D,Sketch037,Pad014,Sketch038,Pad015,Sketch039,Pocket013]
  Origin = -> Origin010
  Tip = -> Pocket013
FEATURE [Part::Part2DObjectPython] Clone2D001  label="Sketch029 (2D)001"  # Draft 2D object (typed FeaturePython)
  Fuse = false
  Objects = -> [Sketch029]
  Scale = (1,1,1)
FEATURE [Sketcher::SketchObject] Sketch040
  ArcFitTolerance = 1e-06
  AttachmentSupport = -> [XY_Plane011]
  ExternalGeometry = -> [Clone2D001]
  FullyConstrained = true
  MakeInternals = false
  MapMode = 5
  sketch-geometry (6):
    g0: ArcOfCircle CenterX=0 CenterY=-9.5 CenterZ=0 NormalX=0 NormalY=0 NormalZ=1 AngleXU=0 Radius=5.15 StartAngle=0.195416 EndAngle=2.94618
    g1: LineSegment StartX=-14 StartY=-0.5 StartZ=0 EndX=-14 EndY=-8.5 EndZ=0
    g2: LineSegment StartX=-14 StartY=-8.5 StartZ=0 EndX=-5.05198 EndY=-8.5 EndZ=0
    g3: LineSegment StartX=-14 StartY=-0.5 StartZ=0 EndX=14 EndY=-0.5 EndZ=0
    g4: LineSegment StartX=14 StartY=-0.5 StartZ=0 EndX=14 EndY=-8.5 EndZ=0
    g5: LineSegment StartX=14 StartY=-8.5 StartZ=0 EndX=5.05198 EndY=-8.5 EndZ=0
  constraints (17):
    c: Coincident(g0,g-3)
    c: Horizontal(g0,g0)
    c: DistanceY(g0,g0) = 1
    c: Vertical(g1)
    c: Coincident(g1,g2)
    c: Coincident(g2,g0)
    c: Horizontal(g2)
    c: Coincident(g1,g3)
    c: Coincident(g3,g4)
    c: Vertical(g4)
    c: Coincident(g4,g5)
    c: Coincident(g5,g0)
    c: Horizontal(g5)
    c: Equal(g-3,g0)
    c: DistanceY(g4,g4) = 8
    c: Symmetric(g3,g1,g-2)
    c: DistanceX(g3,g3) = 28
FEATURE [PartDesign::Pad] Pad016
  Direction = (0,0,1)
  Length = 9.7
  Length2 = 10
  Profile = -> Sketch040
  ReferenceAxis = -> Sketch040 [N_Axis]
  Suppressed = false
  Type = 0
FEATURE [Sketcher::SketchObject] Sketch041
  ArcFitTolerance = 1e-06
  AttachmentSupport = -> [XZ_Plane011]
  ExternalGeometry = -> [Pad015]
  FullyConstrained = true
  MakeInternals = false
  MapMode = 5
  Placement = pos=(0,0,0) rot=(1,0,0;1.5708rad)
  sketch-geometry (5):
    g0: Circle CenterX=-8.02599 CenterY=5 CenterZ=0 NormalX=0 NormalY=0 NormalZ=1 AngleXU=0 Radius=1.65
    g1: Circle CenterX=8.02599 CenterY=5 CenterZ=0 NormalX=0 NormalY=0 NormalZ=1 AngleXU=0 Radius=1.65
    g2: LineSegment [constr] StartX=-11 StartY=5 StartZ=0 EndX=-5.05198 EndY=5 EndZ=0
    g3: LineSegment [constr] StartX=-11 StartY=10 StartZ=0 EndX=-5.05198 EndY=10 EndZ=0
    g4: LineSegment [constr] StartX=-8.02599 StartY=10 StartZ=0 EndX=-8.02599 EndY=5 EndZ=0
  constraints (11):
    c: Symmetric(g1,g0,g-2)
    c: Symmetric(g-3,g-3,g2)
    c: Symmetric(g-4,g-4,g2)
    c: PointOnObject(g0,g2)
    c: Coincident(g3,g-3)
    c: Coincident(g3,g-4)
    c: Symmetric(g3,g3,g4)
    c: Coincident(g4,g0)
    c: Vertical(g4)
    c: Equal(g0,g1)
    c: Diameter(g0) = 3.3
FEATURE [PartDesign::Pocket] Pocket014  label="ScrewHolePocket014"
  BaseFeature = -> Pad016
  Direction = (0,1,-2e-16)
  Length = 5
  Length2 = 5
  Midplane = true
  Profile = -> Sketch041
  ReferenceAxis = -> Sketch041 [N_Axis]
  Suppressed = false
  Type = 1
FEATURE [Sketcher::SketchObject] Sketch042
  ArcFitTolerance = 1e-06
  AttachmentSupport = -> [Pocket014]
  ExternalGeometry = -> [Pocket014]
  FullyConstrained = true
  MakeInternals = false
  MapMode = 5
  Placement = pos=(0,0,9.7) rot=(0,0,1;0rad)
  sketch-geometry (5):
    g0: LineSegment StartX=-10.926 StartY=-2.5 StartZ=0 EndX=-10.926 EndY=-5.2 EndZ=0
    g1: LineSegment StartX=-10.926 StartY=-5.2 StartZ=0 EndX=-5.12599 EndY=-5.2 EndZ=0
    g2: LineSegment StartX=-5.12599 StartY=-5.2 StartZ=0 EndX=-5.12599 EndY=-2.5 EndZ=0
    g3: LineSegment StartX=-5.12599 StartY=-2.5 StartZ=0 EndX=-10.926 EndY=-2.5 EndZ=0
    g4: LineSegment [constr] StartX=-8.02599 StartY=-8.5 StartZ=0 EndX=-8.02599 EndY=-5.2 EndZ=0
  constraints (14):
    c: Coincident(g0,g1)
    c: Coincident(g1,g2)
    c: Coincident(g2,g3)
    c: Coincident(g3,g0)
    c: Vertical(g0)
    c: Vertical(g2)
    c: Horizontal(g1)
    c: Horizontal(g3)
    c: DistanceX(g3,g3) = 5.8
    c: Symmetric(g-3,g-3,g4)
    c: PointOnObject(g4,g1)
    c: Symmetric(g0,g1,g4)
    c: DistanceY(g0,g0) = 2.7
    c: DistanceY(g0,g-4) = 2
FEATURE [PartDesign::Pocket] Pocket015
  BaseFeature = -> Pocket014
  Direction = (0,0,-1)
  Length = 8.3
  Length2 = 5
  Profile = -> Sketch042
  ReferenceAxis = -> Sketch042 [N_Axis]
  Suppressed = false
  Type = 0
FEATURE [PartDesign::Mirrored] Mirrored001
  BaseFeature = -> Pocket015
  MirrorPlane = -> Sketch042 [V_Axis]
  Originals = -> [Pocket015]
  Suppressed = false
  TransformMode = 0
FEATURE [PartDesign::Body] Body011  label="SlidingBodyBrakePad"
  AllowCompound = false
  Group = -> [Clone2D001,Sketch040,Pad016,Sketch041,Pocket014,Sketch042,Pocket015,Mirrored001]
  Origin = -> Origin011
  Tip = -> Mirrored001
FEATURE [Sketcher::SketchObject] Sketch043
  ArcFitTolerance = 1e-06
  AttachmentSupport = -> [XY_Plane012]
  FullyConstrained = true
  MakeInternals = false
  MapMode = 5
  sketch-geometry (2):
    g0: Circle CenterX=0 CenterY=0 CenterZ=0 NormalX=0 NormalY=0 NormalZ=1 AngleXU=0 Radius=5
    g1: Circle CenterX=0 CenterY=0 CenterZ=0 NormalX=0 NormalY=0 NormalZ=1 AngleXU=0 Radius=4
  constraints (4):
    c: Coincident(g0,g-1)
    c: Coincident(g1,g0)
    c: Diameter(g0) = 10
    c: Diameter(g1) = 8
FEATURE [PartDesign::Pad] Pad017
  Direction = (0,0,1)
  Length = 250
  Length2 = 10
  Profile = -> Sketch043
  ReferenceAxis = -> Sketch043 [N_Axis]
  Suppressed = false
  Type = 0
FEATURE [PartDesign::Body] Body012  label="Rod"
  AllowCompound = false
  Group = -> [Sketch043,Pad017]
  Origin = -> Origin012
  Tip = -> Pad017
FEATURE [App::Link] mountingPlate  label="mountingPlate001"
  LinkedObject = -> Body
FEATURE [App::FeaturePython] GroundedJoint  # Assembly grounded joint (typed FeaturePython)
  ObjectToGround = -> mountingPlate
FEATURE [App::Link] Rod  label="Rod001"
  LinkPlacement = pos=(2.5146,-3.2766,-203.559) rot=(0,0,1;0rad)
  LinkedObject = -> Body012
  Placement = pos=(2.5146,-3.2766,-203.559) rot=(0,0,1;0rad)
FEATURE [App::FeaturePython] Joint  label="RodSlider"  # Assembly joint (typed FeaturePython)
  Activated = true
  AngleMax = 0
  AngleMin = 0
  Detach1 = false
  Detach2 = false
  Distance = 0
  Distance2 = 0
  EnableAngleMax = false
  EnableAngleMin = false
  EnableLengthMax = true
  EnableLengthMin = true
  JointType = 3 (Slider)
  LengthMax = 225
  LengthMin = 175
  Placement2 = pos=(2.5146,-3.2766,0) rot=(0,0,1;0rad)
  Reference1 = -> Assembly [Rod.Edge2,Rod.Edge2]
  Reference2 = -> Assembly [mountingPlate.Edge33,mountingPlate.Edge33]
FEATURE [App::Link] SlidingBodyTop  label="SlidingBodyTop001"
  LinkPlacement = pos=(2.5146,6.2234,-19.17) rot=(0,1,0;3.14159rad)
  LinkedObject = -> Body008
  Placement = pos=(2.5146,6.2234,-19.17) rot=(0,1,0;3.14159rad)
FEATURE [App::Link] Handle  label="Handle001"
  LinkPlacement = pos=(2.5146,-3.2766,-80.1587) rot=(0,0,-1;1.5708rad)
  LinkedObject = -> Body001
  Placement = pos=(2.5146,-3.2766,-80.1587) rot=(0,0,-1;1.5708rad)
FEATURE [App::FeaturePython] Joint001  label="Fixed"  # Assembly joint (typed FeaturePython)
  Activated = true
  AngleMax = 0
  AngleMin = 0
  Detach1 = false
  Detach2 = false
  Distance = 0
  Distance2 = 0
  EnableAngleMax = false
  EnableAngleMin = false
  EnableLengthMax = false
  EnableLengthMin = false
  JointType = 0 (Fixed)
  LengthMax = 0
  LengthMin = 0
  Offset2 = pos=(0,0,25) rot=(0,0,1;1.5708rad)
  Placement1 = pos=(0,0,250) rot=(0,0,1;0rad)
  Placement2 = pos=(0,0,126.6) rot=(0,0,1;1.5708rad)
  Reference1 = -> Assembly [Rod.Edge3,Rod.Edge3]
  Reference2 = -> Assembly [Handle.Edge16,Handle.Edge16]
FEATURE [App::FeaturePython] Joint002  label="Fixed001"  # Assembly joint (typed FeaturePython)
  Activated = true
  AngleMax = 0
  AngleMin = 0
  Detach1 = false
  Detach2 = false
  Distance = 0
  Distance2 = 0
  EnableAngleMax = false
  EnableAngleMin = false
  EnableLengthMax = false
  EnableLengthMin = false
  JointType = 0 (Fixed)
  LengthMax = 0
  LengthMin = 0
  Offset2 = pos=(0,0,-16) rot=(0,0,1;3.14159rad)
  Placement1 = pos=(0,-9.5,0) rot=(0,0,1;0rad)
  Placement2 = pos=(2.5146,-3.2766,-19.17) rot=(0,0,1;3.14159rad)
  Reference1 = -> Assembly [SlidingBodyTop.Edge15,SlidingBodyTop.Edge15]
  Reference2 = -> Assembly [mountingPlate.Edge18,mountingPlate.Edge18]
FEATURE [App::Link] SlidingBodyBottom  label="SlidingBodyBottom001"
  LinkPlacement = pos=(2.5146,6.2234,-87.17) rot=(0,1,0;3.14159rad)
  LinkedObject = -> Body009
  Placement = pos=(2.5146,6.2234,-87.17) rot=(0,1,0;3.14159rad)
FEATURE [App::FeaturePython] Joint003  label="Fixed002"  # Assembly joint (typed FeaturePython)
  Activated = true
  AngleMax = 0
  AngleMin = 0
  Detach1 = false
  Detach2 = false
  Distance = 0
  Distance2 = 0
  EnableAngleMax = false
  EnableAngleMin = false
  EnableLengthMax = false
  EnableLengthMin = false
  JointType = 0 (Fixed)
  LengthMax = 0
  LengthMin = 0
  Offset2 = pos=(0,0,60) rot=(0,0,1;0rad)
  Placement1 = pos=(0,-9.5,-4) rot=(0,0,1;0rad)
  Placement2 = pos=(0,-9.5,64) rot=(0,0,1;0rad)
  Reference1 = -> Assembly [SlidingBodyBottom.Edge70,SlidingBodyBottom.Edge70]
  Reference2 = -> Assembly [SlidingBodyTop.Edge32,SlidingBodyTop.Edge32]
FEATURE [App::Link] SlidingBodyBrakeBase  label="SlidingBodyBrakeBase001"
  LinkPlacement = pos=(2.5146,6.2234,-81.17) rot=(0,0,1;0rad)
  LinkedObject = -> Body010
  Placement = pos=(2.5146,6.2234,-81.17) rot=(0,0,1;0rad)
FEATURE [App::FeaturePython] Joint004  label="Fixed003"  # Assembly joint (typed FeaturePython)
  Activated = true
  AngleMax = 0
  AngleMin = 0
  Detach1 = false
  Detach2 = false
  Distance = 0
  Distance2 = 0
  EnableAngleMax = false
  EnableAngleMin = false
  EnableLengthMax = false
  EnableLengthMin = false
  JointType = 0 (Fixed)
  LengthMax = 0
  LengthMin = 0
  Offset2 = pos=(0,0,0) rot=(0,0,1;3.14159rad)
  Placement1 = pos=(0,-9.5,-4) rot=(0,0,1;0rad)
  Placement2 = pos=(0,-9.5,-2) rot=(0,0,1;3.14159rad)
  Reference1 = -> Assembly [SlidingBodyBottom.Edge70,SlidingBodyBottom.Edge70]
  Reference2 = -> Assembly [SlidingBodyBrakeBase.Edge31,SlidingBodyBrakeBase.Edge31]
FEATURE [App::Link] SlidingBodyBrakePad  label="SlidingBodyBrakePad001"
  LinkPlacement = pos=(2.5146,5.31028,-81.17) rot=(0,0,1;0rad)
  LinkedObject = -> Body011
  Placement = pos=(2.5146,5.31028,-81.17) rot=(0,0,1;0rad)
FEATURE [App::FeaturePython] Joint005  label="BrakePadSlider"  # Assembly joint (typed FeaturePython)
  Activated = true
  AngleMax = 0
  AngleMin = 0
  Detach1 = false
  Detach2 = false
  Distance = 0
  Distance2 = 0
  EnableAngleMax = false
  EnableAngleMin = false
  EnableLengthMax = true
  EnableLengthMin = true
  JointType = 3 (Slider)
  LengthMax = 4
  LengthMin = 0
  Placement1 = pos=(8.02599,-8.5,5) rot=(1,0,0;1.5708rad)
  Placement2 = pos=(8.02599,-10.5,5) rot=(-1,0,0;1.5708rad)
  Reference1 = -> Assembly [SlidingBodyBrakePad.Edge34,SlidingBodyBrakePad.Edge34]
  Reference2 = -> Assembly [SlidingBodyBrakeBase.Edge52,SlidingBodyBrakeBase.Edge52]
FEATURE [App::Link] SlidingStop  label="SlidingStop001"
  LinkPlacement = pos=(2.5146,-3.2766,-121.559) rot=(0,0,1;0rad)
  LinkedObject = -> Body006
  Placement = pos=(2.5146,-3.2766,-121.559) rot=(0,0,1;0rad)
FEATURE [App::FeaturePython] Joint006  label="Fixed004"  # Assembly joint (typed FeaturePython)
  Activated = true
  AngleMax = 0
  AngleMin = 0
  Detach1 = false
  Detach2 = false
  Distance = 0
  Distance2 = 0
  EnableAngleMax = false
  EnableAngleMin = false
  EnableLengthMax = false
  EnableLengthMin = false
  JointType = 0 (Fixed)
  LengthMax = 0
  LengthMin = 0
  Offset2 = pos=(0,0,77) rot=(0,0,1;0rad)
  Placement1 = pos=(0,0,-5) rot=(0,0,1;0rad)
  Placement2 = pos=(0,0,77) rot=(0,0,1;0rad)
  Reference1 = -> Assembly [SlidingStop.Edge6,SlidingStop.Edge6]
  Reference2 = -> Assembly [Rod.Edge2,Rod.Edge2]
FEATURE [App::Link] SwitchActuator  label="SwitchActuator001"
  LinkPlacement = pos=(2.5146,-3.2766,-130.559) rot=(0,1,0;3.14159rad)
  LinkedObject = -> Body007
  Placement = pos=(2.5146,-3.2766,-130.559) rot=(0,1,0;3.14159rad)
FEATURE [App::FeaturePython] Joint007  label="Fixed005"  # Assembly joint (typed FeaturePython)
  Activated = true
  AngleMax = 0
  AngleMin = 0
  Detach1 = false
  Detach2 = false
  Distance = 0
  Distance2 = 0
  EnableAngleMax = false
  EnableAngleMin = false
  EnableLengthMax = false
  EnableLengthMin = false
  JointType = 0 (Fixed)
  LengthMax = 0
  LengthMin = 0
  Offset2 = pos=(0,0,62) rot=(0,0,1;0rad)
  Placement1 = pos=(0,2.2e-15,11) rot=(0,0,1;3.14159rad)
  Placement2 = pos=(0,0,62) rot=(0,0,1;0rad)
  Reference1 = -> Assembly [SwitchActuator.Edge7,SwitchActuator.Edge7]
  Reference2 = -> Assembly [Rod.Edge2,Rod.Edge2]
FEATURE [Assembly::JointGroup] Joints
  Group = -> [GroundedJoint,Joint,Joint001,Joint002,Joint003,Joint004,Joint005,Joint006,Joint007]
FEATURE [Assembly::AssemblyObject] Assembly
  Group = -> [Joints,mountingPlate,GroundedJoint,Rod,Joint,SlidingBodyTop,Handle,Joint001,Joint002,SlidingBodyBottom,Joint003,SlidingBodyBrakeBase,Joint004,SlidingBodyBrakePad,Joint005,SlidingStop,Joint006,SwitchActuator,Joint007]
  Origin = -> Origin013
  Type = Assembly
FEATURE [Sketcher::SketchObject] Sketch044
  ArcFitTolerance = 1e-06
  AttachmentSupport = -> [XZ_Plane014]
  FullyConstrained = true
  MakeInternals = false
  MapMode = 5
  Placement = pos=(0,0,0) rot=(1,0,0;1.5708rad)
  sketch-geometry (6):
    g0: LineSegment StartX=-3 StartY=0 StartZ=0 EndX=-3 EndY=5 EndZ=0
    g1: LineSegment StartX=-3 StartY=5 StartZ=0 EndX=-5.1 EndY=5 EndZ=0
    g2: LineSegment StartX=-5.1 StartY=5 StartZ=0 EndX=-5.1 EndY=3.3 EndZ=0
    g3: LineSegment StartX=-5.1 StartY=3.3 StartZ=0 EndX=-4.1 EndY=3.3 EndZ=0
    g4: LineSegment StartX=-4.1 StartY=3.3 StartZ=0 EndX=-3.9 EndY=0 EndZ=0
    g5: LineSegment StartX=-3.9 StartY=0 StartZ=0 EndX=-3 EndY=0 EndZ=0
  constraints (18):
    c: PointOnObject(g0,g-1)
    c: Vertical(g0)
    c: Coincident(g0,g1)
    c: Horizontal(g1)
    c: Coincident(g1,g2)
    c: Vertical(g2)
    c: Coincident(g2,g3)
    c: Horizontal(g3)
    c: Coincident(g3,g4)
    c: PointOnObject(g4,g-1)
    c: Coincident(g4,g5)
    c: Coincident(g5,g0)
    c: DistanceX(g1,g-1) = 5.1
    c: DistanceX(g3,g3) = 1
    c: DistanceX(g4,g-1) = 3.9
    c: DistanceX(g0,g-1) = 3
    c: DistanceY(g2,g2) = 1.7
    c: DistanceY(g0,g0) = 5
FEATURE [PartDesign::Revolution] Revolution005
  Angle = 360
  Angle2 = 60
  Axis = (0,2e-16,1)
  Base = (0,0,0)
  Placement = pos=(0,0,0) rot=(1,0,0;1.5708rad)
  Profile = -> Sketch044
  ReferenceAxis = -> Sketch044 [V_Axis]
  Suppressed = false
  Type = 0
FEATURE [PartDesign::Chamfer] Chamfer002
  Angle = 45
  Base = -> Revolution005 [Edge4]
  BaseFeature = -> Revolution005
  ChamferType = 0
  FlipDirection = false
  Placement = pos=(0,0,0) rot=(1,0,0;1.5708rad)
  Size = 1
  Size2 = 1
  SupportTransform = false
  Suppressed = false
  UseAllEdges = false
FEATURE [PartDesign::Body] Body013  label="RodCableSafety"
  AllowCompound = false
  Group = -> [Sketch044,Revolution005,Chamfer002]
  Origin = -> Origin014
  Tip = -> Chamfer002
